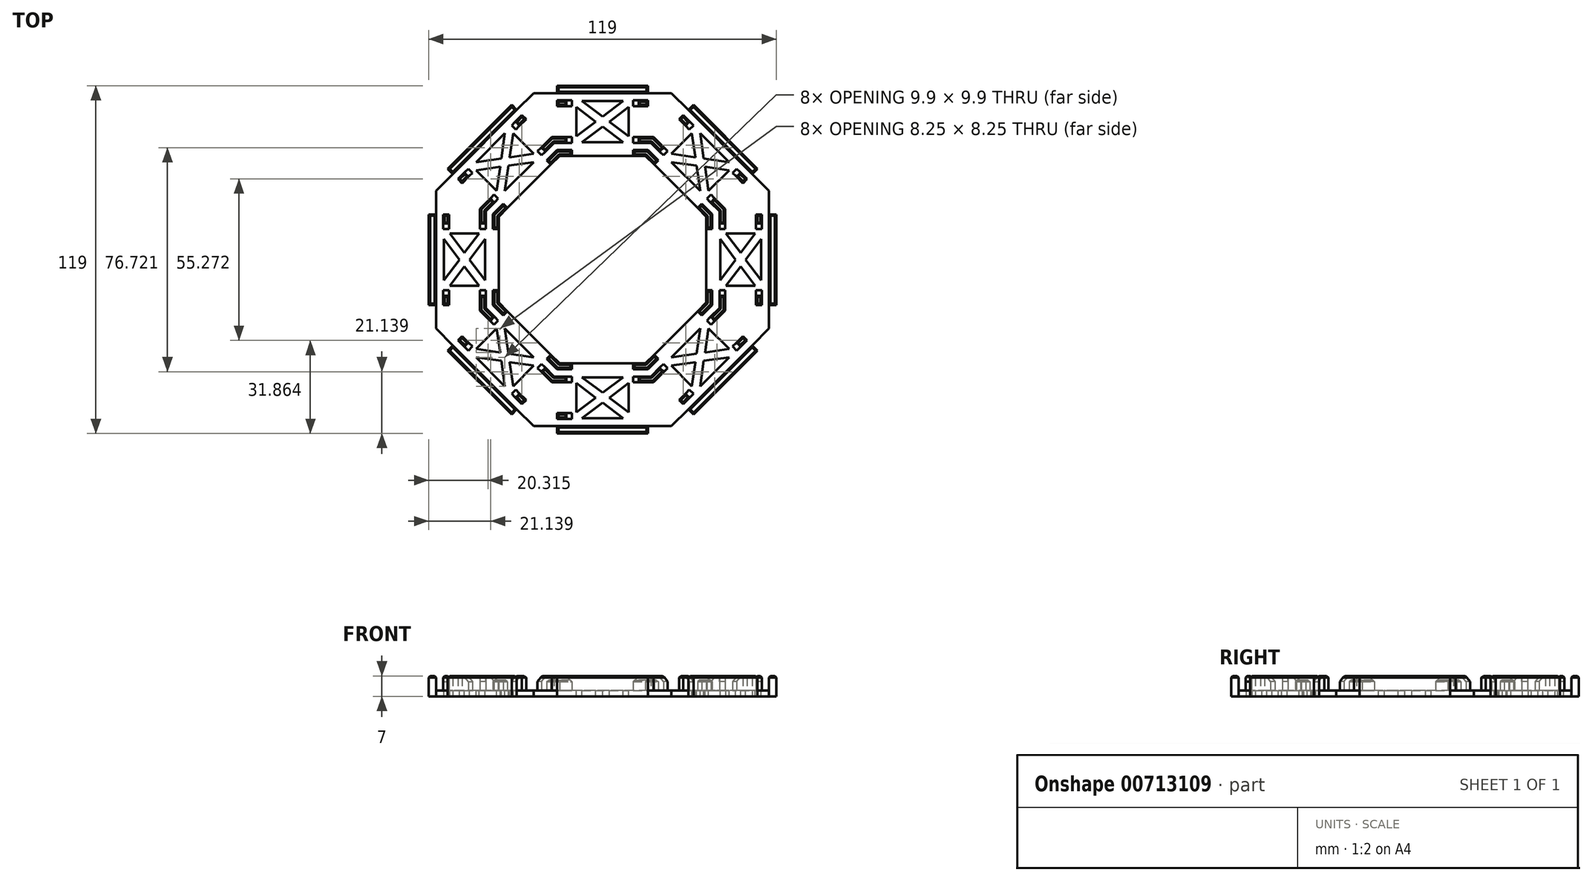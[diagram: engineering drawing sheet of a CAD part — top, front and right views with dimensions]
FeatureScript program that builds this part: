
annotation { "Feature Type Name" : "Feature", "Feature Type Description" : "" }
export const myFeature = defineFeature(function(context is Context, id is Id, definition is map)
    precondition{}
    {
        {
            var Q0;
            Q0=qCreatedBy(makeId("Top.planeOp"),FACE);
            var sketch = newSketch(context, id + "F0", { "sketchPlane" : qUnion([Q0])});
            skLineSegment(sketch, "E0.bottom", {"start": v(15.53, 37.5) * mm, "end": v(-15.53, 37.5) * mm});
            skLineSegment(sketch, "E0.top", {"start": v(15.53, -37.5) * mm, "end": v(-15.53, -37.5) * mm});
            skLineSegment(sketch, "E0.left", {"start": v(37.5, 15.53) * mm, "end": v(37.5, -15.53) * mm});
            skLineSegment(sketch, "E0.right", {"start": v(-37.5, 15.53) * mm, "end": v(-37.5, -15.53) * mm});
            skPoint(sketch, "E0.middle", {"position": v(0, 0) * mm});
            skLineSegment(sketch, "E1.bottom", {"start": v(37.5, 15.53) * mm, "end": v(15.53, 37.5) * mm});
            skLineSegment(sketch, "E1.top", {"start": v(-15.53, -37.5) * mm, "end": v(-37.5, -15.53) * mm});
            skLineSegment(sketch, "E1.left", {"start": v(37.5, -15.53) * mm, "end": v(15.53, -37.5) * mm});
            skLineSegment(sketch, "E1.right", {"start": v(-15.53, 37.5) * mm, "end": v(-37.5, 15.53) * mm});
            skPoint(sketch, "E2.orphan", {"position": v(-37.5, 37.5) * mm});
            skPoint(sketch, "E3.orphan", {"position": v(0, 53.03) * mm});
            skPoint(sketch, "E4.orphan", {"position": v(37.5, 37.5) * mm});
            skPoint(sketch, "E5.orphan", {"position": v(53.03, 0) * mm});
            skPoint(sketch, "E6.orphan", {"position": v(37.5, -37.5) * mm});
            skPoint(sketch, "E7.orphan", {"position": v(0, -53.03) * mm});
            skPoint(sketch, "E8.orphan", {"position": v(-37.5, -37.5) * mm});
            skPoint(sketch, "E9.orphan", {"position": v(-53.03, 0) * mm});
            skLineSegment(sketch, "E10.0", {"start": v(57, 23.61) * mm, "end": v(57, -23.61) * mm});
            skLineSegment(sketch, "E10.1", {"start": v(57, 23.61) * mm, "end": v(23.61, 57) * mm});
            skLineSegment(sketch, "E10.2", {"start": v(57, -23.61) * mm, "end": v(23.61, -57) * mm});
            skLineSegment(sketch, "E10.3", {"start": v(23.61, 57) * mm, "end": v(-23.61, 57) * mm});
            skLineSegment(sketch, "E10.4", {"start": v(23.61, -57) * mm, "end": v(-23.61, -57) * mm});
            skLineSegment(sketch, "E10.5", {"start": v(-23.61, -57) * mm, "end": v(-57, -23.61) * mm});
            skLineSegment(sketch, "E10.6", {"start": v(-57, 23.61) * mm, "end": v(-57, -23.61) * mm});
            skLineSegment(sketch, "E10.7", {"start": v(-23.61, 57) * mm, "end": v(-57, 23.61) * mm});
            skLineSegment(sketch, "E11.0", {"start": v(-16.57, 40) * mm, "end": v(-40, 16.57) * mm});
            skLineSegment(sketch, "E11.1", {"start": v(16.57, 40) * mm, "end": v(-16.57, 40) * mm});
            skLineSegment(sketch, "E11.2", {"start": v(-40, 16.57) * mm, "end": v(-40, -16.57) * mm});
            skLineSegment(sketch, "E11.3", {"start": v(40, 16.57) * mm, "end": v(16.57, 40) * mm});
            skLineSegment(sketch, "E11.4", {"start": v(-16.57, -40) * mm, "end": v(-40, -16.57) * mm});
            skLineSegment(sketch, "E11.5", {"start": v(16.57, -40) * mm, "end": v(-16.57, -40) * mm});
            skLineSegment(sketch, "E11.6", {"start": v(40, -16.57) * mm, "end": v(16.57, -40) * mm});
            skLineSegment(sketch, "E11.7", {"start": v(40, 16.57) * mm, "end": v(40, -16.57) * mm});
            skLineSegment(sketch, "E12.0", {"start": v(14.7, 35.5) * mm, "end": v(-14.7, 35.5) * mm});
            skLineSegment(sketch, "E12.1", {"start": v(35.5, 14.7) * mm, "end": v(14.7, 35.5) * mm});
            skLineSegment(sketch, "E12.2", {"start": v(-14.7, 35.5) * mm, "end": v(-35.5, 14.7) * mm});
            skLineSegment(sketch, "E12.3", {"start": v(35.5, 14.7) * mm, "end": v(35.5, -14.7) * mm});
            skLineSegment(sketch, "E12.4", {"start": v(-35.5, 14.7) * mm, "end": v(-35.5, -14.7) * mm});
            skLineSegment(sketch, "E12.5", {"start": v(-14.7, -35.5) * mm, "end": v(-35.5, -14.7) * mm});
            skLineSegment(sketch, "E12.6", {"start": v(14.7, -35.5) * mm, "end": v(-14.7, -35.5) * mm});
            skLineSegment(sketch, "E12.7", {"start": v(35.5, -14.7) * mm, "end": v(14.7, -35.5) * mm});
            skLineSegment(sketch, "E13.0", {"start": v(-17.4, 42) * mm, "end": v(-42, 17.4) * mm});
            skLineSegment(sketch, "E13.1", {"start": v(17.4, 42) * mm, "end": v(-17.4, 42) * mm});
            skLineSegment(sketch, "E13.2", {"start": v(-42, 17.4) * mm, "end": v(-42, -17.4) * mm});
            skLineSegment(sketch, "E13.3", {"start": v(42, 17.4) * mm, "end": v(17.4, 42) * mm});
            skLineSegment(sketch, "E13.4", {"start": v(-17.4, -42) * mm, "end": v(-42, -17.4) * mm});
            skLineSegment(sketch, "E13.5", {"start": v(17.4, -42) * mm, "end": v(-17.4, -42) * mm});
            skLineSegment(sketch, "E13.6", {"start": v(42, -17.4) * mm, "end": v(17.4, -42) * mm});
            skLineSegment(sketch, "E13.7", {"start": v(42, 17.4) * mm, "end": v(42, -17.4) * mm});
            skLineSegment(sketch, "E14.bottom", {"start": v(-10.5, -34.32) * mm, "end": v(10.5, -34.32) * mm});
            skLineSegment(sketch, "E14.top", {"start": v(-10.5, -45.68) * mm, "end": v(10.5, -45.68) * mm});
            skLineSegment(sketch, "E14.left", {"start": v(-10.5, -34.32) * mm, "end": v(-10.5, -45.68) * mm});
            skLineSegment(sketch, "E14.right", {"start": v(10.5, -34.32) * mm, "end": v(10.5, -45.68) * mm});
            skPoint(sketch, "E14.middle", {"position": v(0, -40) * mm});
            skLineSegment(sketch, "E15.1.0", {"start": v(16.85, -31.7) * mm, "end": v(31.7, -16.85) * mm});
            skLineSegment(sketch, "E15.1.1", {"start": v(16.85, -31.7) * mm, "end": v(24.87, -39.72) * mm});
            skLineSegment(sketch, "E15.1.2", {"start": v(24.87, -39.72) * mm, "end": v(39.72, -24.87) * mm});
            skLineSegment(sketch, "E15.1.3", {"start": v(31.7, -16.85) * mm, "end": v(39.72, -24.87) * mm});
            skLineSegment(sketch, "E15.2.0", {"start": v(34.32, -10.5) * mm, "end": v(34.32, 10.5) * mm});
            skLineSegment(sketch, "E15.2.1", {"start": v(34.32, -10.5) * mm, "end": v(45.68, -10.5) * mm});
            skLineSegment(sketch, "E15.2.2", {"start": v(45.68, -10.5) * mm, "end": v(45.68, 10.5) * mm});
            skLineSegment(sketch, "E15.2.3", {"start": v(34.32, 10.5) * mm, "end": v(45.68, 10.5) * mm});
            skLineSegment(sketch, "E16.1.3.0", {"start": v(31.7, 16.85) * mm, "end": v(16.85, 31.7) * mm});
            skLineSegment(sketch, "E16.3.3.0", {"start": v(31.7, 16.85) * mm, "end": v(39.72, 24.87) * mm});
            skLineSegment(sketch, "E16.6.3.0", {"start": v(39.72, 24.87) * mm, "end": v(24.87, 39.72) * mm});
            skLineSegment(sketch, "E16.9.3.0", {"start": v(16.85, 31.7) * mm, "end": v(24.87, 39.72) * mm});
            skLineSegment(sketch, "E16.1.4.0", {"start": v(10.5, 34.32) * mm, "end": v(-10.5, 34.32) * mm});
            skLineSegment(sketch, "E16.3.4.0", {"start": v(10.5, 34.32) * mm, "end": v(10.5, 45.68) * mm});
            skLineSegment(sketch, "E16.6.4.0", {"start": v(10.5, 45.68) * mm, "end": v(-10.5, 45.68) * mm});
            skLineSegment(sketch, "E16.9.4.0", {"start": v(-10.5, 34.32) * mm, "end": v(-10.5, 45.68) * mm});
            skLineSegment(sketch, "E16.1.5.0", {"start": v(-16.85, 31.7) * mm, "end": v(-31.7, 16.85) * mm});
            skLineSegment(sketch, "E16.3.5.0", {"start": v(-16.85, 31.7) * mm, "end": v(-24.87, 39.72) * mm});
            skLineSegment(sketch, "E16.6.5.0", {"start": v(-24.87, 39.72) * mm, "end": v(-39.72, 24.87) * mm});
            skLineSegment(sketch, "E16.9.5.0", {"start": v(-31.7, 16.85) * mm, "end": v(-39.72, 24.87) * mm});
            skLineSegment(sketch, "E16.1.6.0", {"start": v(-34.32, 10.5) * mm, "end": v(-34.32, -10.5) * mm});
            skLineSegment(sketch, "E16.3.6.0", {"start": v(-34.32, 10.5) * mm, "end": v(-45.68, 10.5) * mm});
            skLineSegment(sketch, "E16.6.6.0", {"start": v(-45.68, 10.5) * mm, "end": v(-45.68, -10.5) * mm});
            skLineSegment(sketch, "E16.9.6.0", {"start": v(-34.32, -10.5) * mm, "end": v(-45.68, -10.5) * mm});
            skLineSegment(sketch, "E16.1.7.0", {"start": v(-31.7, -16.85) * mm, "end": v(-16.85, -31.7) * mm});
            skLineSegment(sketch, "E16.3.7.0", {"start": v(-31.7, -16.85) * mm, "end": v(-39.72, -24.87) * mm});
            skLineSegment(sketch, "E16.6.7.0", {"start": v(-39.72, -24.87) * mm, "end": v(-24.87, -39.72) * mm});
            skLineSegment(sketch, "E16.9.7.0", {"start": v(-16.85, -31.7) * mm, "end": v(-24.87, -39.72) * mm});
            skSolve(sketch);
        }
        {
            var Q0;
            {var subQ0=sQuery(id+"F0.wireOp",EDGE,"E16.3.5.0");var subQ1=sQuery(id+"F0.wireOp",EDGE,"E11.0");var subQ2=makeQuery(id+"F0.imprint","INTERSECT",VERTEX,{"derivedFrom":[subQ1,subQ0]});Q0=makeQuery(id+"F0.imprint","IMPRINT",FACE,{"disambiguationData":[TD([[makeQuery(id+"F0.imprint","IMPRINT",EDGE,{"disambiguationData":[TD([[subQ2,-1.0]])],"derivedFrom":subQ1}),-1.0]])]});}
            var Q1;
            {var subQ0=sQuery(id+"F0.wireOp",EDGE,"E15.2.3");var subQ1=sQuery(id+"F0.wireOp",EDGE,"E0.left");var subQ2=makeQuery(id+"F0.imprint","INTERSECT",VERTEX,{"derivedFrom":[subQ1,subQ0]});Q1=makeQuery(id+"F0.imprint","IMPRINT",FACE,{"disambiguationData":[TD([[makeQuery(id+"F0.imprint","IMPRINT",EDGE,{"disambiguationData":[TD([[subQ2,-1.0]])],"derivedFrom":subQ1}),-1.0]])]});}
            var Q2;
            {var subQ5=sQuery(id+"F0.wireOp",EDGE,"E1.bottom");var subQ6=sQuery(id+"F0.wireOp",EDGE,"E0.left");var subQ7=makeQuery(id+"F0.imprint","INTERSECT",VERTEX,{"derivedFrom":[subQ6,subQ5]});Q2=makeQuery(id+"F0.imprint","IMPRINT",FACE,{"disambiguationData":[TD([[makeQuery(id+"F0.imprint","IMPRINT",EDGE,{"disambiguationData":[TD([[subQ7,-1.0]])],"derivedFrom":subQ6}),1.0]])]});}
            var Q3;
            {var subQ0=sQuery(id+"F0.wireOp",EDGE,"E16.3.3.0");var subQ1=sQuery(id+"F0.wireOp",EDGE,"E11.3");var subQ2=makeQuery(id+"F0.imprint","INTERSECT",VERTEX,{"derivedFrom":[subQ1,subQ0]});Q3=makeQuery(id+"F0.imprint","IMPRINT",FACE,{"disambiguationData":[TD([[makeQuery(id+"F0.imprint","IMPRINT",EDGE,{"disambiguationData":[TD([[subQ2,-1.0]])],"derivedFrom":subQ1}),-1.0]])]});}
            var Q4;
            {var subQ0=sQuery(id+"F0.wireOp",EDGE,"E16.3.3.0");var subQ1=sQuery(id+"F0.wireOp",EDGE,"E1.bottom");var subQ2=makeQuery(id+"F0.imprint","INTERSECT",VERTEX,{"derivedFrom":[subQ1,subQ0]});Q4=makeQuery(id+"F0.imprint","IMPRINT",FACE,{"disambiguationData":[TD([[makeQuery(id+"F0.imprint","IMPRINT",EDGE,{"disambiguationData":[TD([[subQ2,-1.0]])],"derivedFrom":subQ1}),1.0]])]});}
            var Q5;
            {var subQ0=sQuery(id+"F0.wireOp",EDGE,"E16.3.3.0");var subQ1=sQuery(id+"F0.wireOp",EDGE,"E1.bottom");var subQ2=makeQuery(id+"F0.imprint","INTERSECT",VERTEX,{"derivedFrom":[subQ1,subQ0]});Q5=makeQuery(id+"F0.imprint","IMPRINT",FACE,{"disambiguationData":[TD([[makeQuery(id+"F0.imprint","IMPRINT",EDGE,{"disambiguationData":[TD([[subQ2,-1.0]])],"derivedFrom":subQ1}),-1.0]])]});}
            var Q6;
            {var subQ5=sQuery(id+"F0.wireOp",EDGE,"E16.6.6.0");Q6=makeQuery(id+"F0.imprint","IMPRINT",FACE,{"disambiguationData":[TD([[makeQuery(id+"F0.imprint","IMPRINT",EDGE,{"derivedFrom":subQ5}),1.0]])]});}
            var Q7;
            {var subQ5=sQuery(id+"F0.wireOp",EDGE,"E0.right");var subQ7=sQuery(id+"F0.wireOp",EDGE,"E1.right");var subQ8=makeQuery(id+"F0.imprint","INTERSECT",VERTEX,{"derivedFrom":[subQ5,subQ7]});Q7=makeQuery(id+"F0.imprint","IMPRINT",FACE,{"disambiguationData":[TD([[makeQuery(id+"F0.imprint","IMPRINT",EDGE,{"disambiguationData":[TD([[subQ8,-1.0]])],"derivedFrom":subQ5}),1.0]])]});}
            var Q8;
            {var subQ0=sQuery(id+"F0.wireOp",EDGE,"E16.3.5.0");var subQ1=sQuery(id+"F0.wireOp",EDGE,"E1.right");var subQ2=makeQuery(id+"F0.imprint","INTERSECT",VERTEX,{"derivedFrom":[subQ1,subQ0]});Q8=makeQuery(id+"F0.imprint","IMPRINT",FACE,{"disambiguationData":[TD([[makeQuery(id+"F0.imprint","IMPRINT",EDGE,{"disambiguationData":[TD([[subQ2,-1.0]])],"derivedFrom":subQ1}),1.0]])]});}
            var Q9;
            {var subQ5=sQuery(id+"F0.wireOp",EDGE,"E15.2.2");Q9=makeQuery(id+"F0.imprint","IMPRINT",FACE,{"disambiguationData":[TD([[makeQuery(id+"F0.imprint","IMPRINT",EDGE,{"derivedFrom":subQ5}),1.0]])]});}
            var Q10;
            {var subQ0=sQuery(id+"F0.wireOp",EDGE,"E16.3.6.0");var subQ1=sQuery(id+"F0.wireOp",EDGE,"E11.2");var subQ2=makeQuery(id+"F0.imprint","INTERSECT",VERTEX,{"derivedFrom":[subQ1,subQ0]});Q10=makeQuery(id+"F0.imprint","IMPRINT",FACE,{"disambiguationData":[TD([[makeQuery(id+"F0.imprint","IMPRINT",EDGE,{"disambiguationData":[TD([[subQ2,-1.0]])],"derivedFrom":subQ1}),-1.0]])]});}
            var Q11;
            {var subQ7=sQuery(id+"F0.wireOp",EDGE,"E1.bottom");var subQ8=sQuery(id+"F0.wireOp",EDGE,"E0.bottom");var subQ9=makeQuery(id+"F0.imprint","INTERSECT",VERTEX,{"derivedFrom":[subQ8,subQ7]});Q11=makeQuery(id+"F0.imprint","IMPRINT",FACE,{"disambiguationData":[TD([[makeQuery(id+"F0.imprint","IMPRINT",EDGE,{"disambiguationData":[TD([[subQ9,-1.0]])],"derivedFrom":subQ8}),1.0]])]});}
            var Q12;
            {var subQ5=sQuery(id+"F0.wireOp",EDGE,"E16.6.4.0");Q12=makeQuery(id+"F0.imprint","IMPRINT",FACE,{"disambiguationData":[TD([[makeQuery(id+"F0.imprint","IMPRINT",EDGE,{"derivedFrom":subQ5}),1.0]])]});}
            var Q13;
            {var subQ0=sQuery(id+"F0.wireOp",EDGE,"E16.3.4.0");var subQ1=sQuery(id+"F0.wireOp",EDGE,"E11.1");var subQ2=makeQuery(id+"F0.imprint","INTERSECT",VERTEX,{"derivedFrom":[subQ1,subQ0]});Q13=makeQuery(id+"F0.imprint","IMPRINT",FACE,{"disambiguationData":[TD([[makeQuery(id+"F0.imprint","IMPRINT",EDGE,{"disambiguationData":[TD([[subQ2,-1.0]])],"derivedFrom":subQ1}),-1.0]])]});}
            var Q14;
            {var subQ5=sQuery(id+"F0.wireOp",EDGE,"E16.6.3.0");Q14=makeQuery(id+"F0.imprint","IMPRINT",FACE,{"disambiguationData":[TD([[makeQuery(id+"F0.imprint","IMPRINT",EDGE,{"derivedFrom":subQ5}),1.0]])]});}
            var Q15;
            {var subQ5=sQuery(id+"F0.wireOp",EDGE,"E1.right");var subQ6=sQuery(id+"F0.wireOp",EDGE,"E0.right");var subQ7=makeQuery(id+"F0.imprint","INTERSECT",VERTEX,{"derivedFrom":[subQ6,subQ5]});Q15=makeQuery(id+"F0.imprint","IMPRINT",FACE,{"disambiguationData":[TD([[makeQuery(id+"F0.imprint","IMPRINT",EDGE,{"disambiguationData":[TD([[subQ7,-1.0]])],"derivedFrom":subQ6}),-1.0]])]});}
            var Q16;
            {var subQ0=sQuery(id+"F0.wireOp",EDGE,"E16.3.4.0");var subQ1=sQuery(id+"F0.wireOp",EDGE,"E0.bottom");var subQ2=makeQuery(id+"F0.imprint","INTERSECT",VERTEX,{"derivedFrom":[subQ1,subQ0]});Q16=makeQuery(id+"F0.imprint","IMPRINT",FACE,{"disambiguationData":[TD([[makeQuery(id+"F0.imprint","IMPRINT",EDGE,{"disambiguationData":[TD([[subQ2,-1.0]])],"derivedFrom":subQ1}),1.0]])]});}
            var Q17;
            {var subQ0=sQuery(id+"F0.wireOp",EDGE,"E16.3.6.0");var subQ1=sQuery(id+"F0.wireOp",EDGE,"E0.right");var subQ2=makeQuery(id+"F0.imprint","INTERSECT",VERTEX,{"derivedFrom":[subQ1,subQ0]});Q17=makeQuery(id+"F0.imprint","IMPRINT",FACE,{"disambiguationData":[TD([[makeQuery(id+"F0.imprint","IMPRINT",EDGE,{"disambiguationData":[TD([[subQ2,-1.0]])],"derivedFrom":subQ1}),1.0]])]});}
            var Q18;
            {var subQ6=sQuery(id+"F0.wireOp",EDGE,"E11.0");var subQ9=sQuery(id+"F0.wireOp",EDGE,"E11.2");var subQ10=makeQuery(id+"F0.imprint","INTERSECT",VERTEX,{"derivedFrom":[subQ6,subQ9]});Q18=makeQuery(id+"F0.imprint","IMPRINT",FACE,{"disambiguationData":[TD([[makeQuery(id+"F0.imprint","IMPRINT",EDGE,{"disambiguationData":[TD([[subQ10,1.0]])],"derivedFrom":subQ6}),-1.0]])]});}
            var Q19;
            {var subQ0=sQuery(id+"F0.wireOp",EDGE,"E16.3.4.0");var subQ1=sQuery(id+"F0.wireOp",EDGE,"E0.bottom");var subQ2=makeQuery(id+"F0.imprint","INTERSECT",VERTEX,{"derivedFrom":[subQ1,subQ0]});Q19=makeQuery(id+"F0.imprint","IMPRINT",FACE,{"disambiguationData":[TD([[makeQuery(id+"F0.imprint","IMPRINT",EDGE,{"disambiguationData":[TD([[subQ2,-1.0]])],"derivedFrom":subQ1}),-1.0]])]});}
            var Q20;
            {var subQ0=sQuery(id+"F0.wireOp",EDGE,"E1.right");var subQ1=sQuery(id+"F0.wireOp",EDGE,"E0.bottom");var subQ2=makeQuery(id+"F0.imprint","INTERSECT",VERTEX,{"derivedFrom":[subQ1,subQ0]});Q20=makeQuery(id+"F0.imprint","IMPRINT",FACE,{"disambiguationData":[TD([[makeQuery(id+"F0.imprint","IMPRINT",EDGE,{"disambiguationData":[TD([[subQ2,1.0]])],"derivedFrom":subQ1}),-1.0]])]});}
            var Q21;
            {var subQ7=sQuery(id+"F0.wireOp",EDGE,"E11.3");var subQ8=sQuery(id+"F0.wireOp",EDGE,"E11.1");var subQ9=makeQuery(id+"F0.imprint","INTERSECT",VERTEX,{"derivedFrom":[subQ8,subQ7]});Q21=makeQuery(id+"F0.imprint","IMPRINT",FACE,{"disambiguationData":[TD([[makeQuery(id+"F0.imprint","IMPRINT",EDGE,{"disambiguationData":[TD([[subQ9,-1.0]])],"derivedFrom":subQ8}),-1.0]])]});}
            var Q22;
            {var subQ5=sQuery(id+"F0.wireOp",EDGE,"E11.1");var subQ9=sQuery(id+"F0.wireOp",EDGE,"E11.0");var subQ11=makeQuery(id+"F0.imprint","INTERSECT",VERTEX,{"derivedFrom":[subQ9,subQ5]});Q22=makeQuery(id+"F0.imprint","IMPRINT",FACE,{"disambiguationData":[TD([[makeQuery(id+"F0.imprint","IMPRINT",EDGE,{"disambiguationData":[TD([[subQ11,-1.0]])],"derivedFrom":subQ9}),-1.0]])]});}
            var Q23;
            {var subQ5=sQuery(id+"F0.wireOp",EDGE,"E1.bottom");var subQ6=sQuery(id+"F0.wireOp",EDGE,"E0.bottom");var subQ7=makeQuery(id+"F0.imprint","INTERSECT",VERTEX,{"derivedFrom":[subQ6,subQ5]});Q23=makeQuery(id+"F0.imprint","IMPRINT",FACE,{"disambiguationData":[TD([[makeQuery(id+"F0.imprint","IMPRINT",EDGE,{"disambiguationData":[TD([[subQ7,-1.0]])],"derivedFrom":subQ6}),-1.0]])]});}
            var Q24;
            {var subQ0=sQuery(id+"F0.wireOp",EDGE,"E16.3.5.0");var subQ1=sQuery(id+"F0.wireOp",EDGE,"E1.right");var subQ2=makeQuery(id+"F0.imprint","INTERSECT",VERTEX,{"derivedFrom":[subQ1,subQ0]});Q24=makeQuery(id+"F0.imprint","IMPRINT",FACE,{"disambiguationData":[TD([[makeQuery(id+"F0.imprint","IMPRINT",EDGE,{"disambiguationData":[TD([[subQ2,-1.0]])],"derivedFrom":subQ1}),-1.0]])]});}
            var Q25;
            {var subQ5=sQuery(id+"F0.wireOp",EDGE,"E11.3");var subQ7=sQuery(id+"F0.wireOp",EDGE,"E11.7");var subQ8=makeQuery(id+"F0.imprint","INTERSECT",VERTEX,{"derivedFrom":[subQ5,subQ7]});Q25=makeQuery(id+"F0.imprint","IMPRINT",FACE,{"disambiguationData":[TD([[makeQuery(id+"F0.imprint","IMPRINT",EDGE,{"disambiguationData":[TD([[subQ8,-1.0]])],"derivedFrom":subQ5}),-1.0]])]});}
            var Q26;
            {var subQ0=sQuery(id+"F0.wireOp",EDGE,"E15.2.3");var subQ1=sQuery(id+"F0.wireOp",EDGE,"E11.7");var subQ2=makeQuery(id+"F0.imprint","INTERSECT",VERTEX,{"derivedFrom":[subQ1,subQ0]});Q26=makeQuery(id+"F0.imprint","IMPRINT",FACE,{"disambiguationData":[TD([[makeQuery(id+"F0.imprint","IMPRINT",EDGE,{"disambiguationData":[TD([[subQ2,-1.0]])],"derivedFrom":subQ1}),1.0]])]});}
            var Q27;
            {var subQ5=sQuery(id+"F0.wireOp",EDGE,"E16.6.5.0");Q27=makeQuery(id+"F0.imprint","IMPRINT",FACE,{"disambiguationData":[TD([[makeQuery(id+"F0.imprint","IMPRINT",EDGE,{"derivedFrom":subQ5}),1.0]])]});}
            var Q28;
            Q28=makeQuery(id+"F0.imprint","IMPRINT",FACE,{"disambiguationData":[TD([[makeQuery(id+"F0.imprint","IMPRINT",EDGE,{"derivedFrom":sQuery(id+"F0.wireOp",EDGE,"E10.0")}),-1.0]])]});
            var Q29;
            {var subQ0=sQuery(id+"F0.wireOp",EDGE,"E15.2.3");var subQ1=sQuery(id+"F0.wireOp",EDGE,"E0.left");var subQ2=makeQuery(id+"F0.imprint","INTERSECT",VERTEX,{"derivedFrom":[subQ1,subQ0]});Q29=makeQuery(id+"F0.imprint","IMPRINT",FACE,{"disambiguationData":[TD([[makeQuery(id+"F0.imprint","IMPRINT",EDGE,{"disambiguationData":[TD([[subQ2,-1.0]])],"derivedFrom":subQ1}),1.0]])]});}
            var Q30;
            {var subQ6=sQuery(id+"F0.wireOp",EDGE,"E1.bottom");var subQ9=sQuery(id+"F0.wireOp",EDGE,"E0.left");var subQ11=makeQuery(id+"F0.imprint","INTERSECT",VERTEX,{"derivedFrom":[subQ9,subQ6]});Q30=makeQuery(id+"F0.imprint","IMPRINT",FACE,{"disambiguationData":[TD([[makeQuery(id+"F0.imprint","IMPRINT",EDGE,{"disambiguationData":[TD([[subQ11,-1.0]])],"derivedFrom":subQ9}),-1.0]])]});}
            var Q31;
            {var subQ0=sQuery(id+"F0.wireOp",EDGE,"E16.3.6.0");var subQ1=sQuery(id+"F0.wireOp",EDGE,"E0.right");var subQ2=makeQuery(id+"F0.imprint","INTERSECT",VERTEX,{"derivedFrom":[subQ1,subQ0]});Q31=makeQuery(id+"F0.imprint","IMPRINT",FACE,{"disambiguationData":[TD([[makeQuery(id+"F0.imprint","IMPRINT",EDGE,{"disambiguationData":[TD([[subQ2,-1.0]])],"derivedFrom":subQ1}),-1.0]])]});}
            var Q32;
            {var subQ5=sQuery(id+"F0.wireOp",EDGE,"E1.right");var subQ6=sQuery(id+"F0.wireOp",EDGE,"E0.bottom");var subQ7=makeQuery(id+"F0.imprint","INTERSECT",VERTEX,{"derivedFrom":[subQ6,subQ5]});Q32=makeQuery(id+"F0.imprint","IMPRINT",FACE,{"disambiguationData":[TD([[makeQuery(id+"F0.imprint","IMPRINT",EDGE,{"disambiguationData":[TD([[subQ7,1.0]])],"derivedFrom":subQ6}),1.0]])]});}
            var Q33;
            {var subQ5=sQuery(id+"F0.wireOp",EDGE,"E14.top");Q33=makeQuery(id+"F0.imprint","IMPRINT",FACE,{"disambiguationData":[TD([[makeQuery(id+"F0.imprint","IMPRINT",EDGE,{"derivedFrom":subQ5}),1.0]])]});}
            var Q34;
            {var subQ0=sQuery(id+"F0.wireOp",EDGE,"E14.right");var subQ1=sQuery(id+"F0.wireOp",EDGE,"E0.top");var subQ2=makeQuery(id+"F0.imprint","INTERSECT",VERTEX,{"derivedFrom":[subQ1,subQ0]});Q34=makeQuery(id+"F0.imprint","IMPRINT",FACE,{"disambiguationData":[TD([[makeQuery(id+"F0.imprint","IMPRINT",EDGE,{"disambiguationData":[TD([[subQ2,-1.0]])],"derivedFrom":subQ1}),1.0]])]});}
            var Q35;
            {var subQ0=sQuery(id+"F0.wireOp",EDGE,"E16.9.7.0");var subQ1=sQuery(id+"F0.wireOp",EDGE,"E1.top");var subQ2=makeQuery(id+"F0.imprint","INTERSECT",VERTEX,{"derivedFrom":[subQ1,subQ0]});Q35=makeQuery(id+"F0.imprint","IMPRINT",FACE,{"disambiguationData":[TD([[makeQuery(id+"F0.imprint","IMPRINT",EDGE,{"disambiguationData":[TD([[subQ2,-1.0]])],"derivedFrom":subQ1}),1.0]])]});}
            var Q36;
            {var subQ0=sQuery(id+"F0.wireOp",EDGE,"E16.9.7.0");var subQ1=sQuery(id+"F0.wireOp",EDGE,"E11.4");var subQ2=makeQuery(id+"F0.imprint","INTERSECT",VERTEX,{"derivedFrom":[subQ1,subQ0]});Q36=makeQuery(id+"F0.imprint","IMPRINT",FACE,{"disambiguationData":[TD([[makeQuery(id+"F0.imprint","IMPRINT",EDGE,{"disambiguationData":[TD([[subQ2,-1.0]])],"derivedFrom":subQ1}),1.0]])]});}
            var Q37;
            {var subQ6=sQuery(id+"F0.wireOp",EDGE,"E0.top");var subQ9=sQuery(id+"F0.wireOp",EDGE,"E1.left");var subQ11=makeQuery(id+"F0.imprint","INTERSECT",VERTEX,{"derivedFrom":[subQ6,subQ9]});Q37=makeQuery(id+"F0.imprint","IMPRINT",FACE,{"disambiguationData":[TD([[makeQuery(id+"F0.imprint","IMPRINT",EDGE,{"disambiguationData":[TD([[subQ11,-1.0]])],"derivedFrom":subQ6}),-1.0]])]});}
            var Q38;
            {var subQ7=sQuery(id+"F0.wireOp",EDGE,"E1.top");var subQ8=sQuery(id+"F0.wireOp",EDGE,"E0.right");var subQ9=makeQuery(id+"F0.imprint","INTERSECT",VERTEX,{"derivedFrom":[subQ8,subQ7]});Q38=makeQuery(id+"F0.imprint","IMPRINT",FACE,{"disambiguationData":[TD([[makeQuery(id+"F0.imprint","IMPRINT",EDGE,{"disambiguationData":[TD([[subQ9,1.0]])],"derivedFrom":subQ8}),1.0]])]});}
            var Q39;
            {var subQ7=sQuery(id+"F0.wireOp",EDGE,"E11.4");var subQ8=sQuery(id+"F0.wireOp",EDGE,"E11.2");var subQ9=makeQuery(id+"F0.imprint","INTERSECT",VERTEX,{"derivedFrom":[subQ8,subQ7]});Q39=makeQuery(id+"F0.imprint","IMPRINT",FACE,{"disambiguationData":[TD([[makeQuery(id+"F0.imprint","IMPRINT",EDGE,{"disambiguationData":[TD([[subQ9,1.0]])],"derivedFrom":subQ8}),-1.0]])]});}
            var Q40;
            {var subQ7=sQuery(id+"F0.wireOp",EDGE,"E11.6");var subQ8=sQuery(id+"F0.wireOp",EDGE,"E11.5");var subQ9=makeQuery(id+"F0.imprint","INTERSECT",VERTEX,{"derivedFrom":[subQ8,subQ7]});Q40=makeQuery(id+"F0.imprint","IMPRINT",FACE,{"disambiguationData":[TD([[makeQuery(id+"F0.imprint","IMPRINT",EDGE,{"disambiguationData":[TD([[subQ9,-1.0]])],"derivedFrom":subQ8}),1.0]])]});}
            var Q41;
            {var subQ5=sQuery(id+"F0.wireOp",EDGE,"E16.6.7.0");Q41=makeQuery(id+"F0.imprint","IMPRINT",FACE,{"disambiguationData":[TD([[makeQuery(id+"F0.imprint","IMPRINT",EDGE,{"derivedFrom":subQ5}),1.0]])]});}
            var Q42;
            {var subQ0=sQuery(id+"F0.wireOp",EDGE,"E14.right");var subQ1=sQuery(id+"F0.wireOp",EDGE,"E0.top");var subQ2=makeQuery(id+"F0.imprint","INTERSECT",VERTEX,{"derivedFrom":[subQ1,subQ0]});Q42=makeQuery(id+"F0.imprint","IMPRINT",FACE,{"disambiguationData":[TD([[makeQuery(id+"F0.imprint","IMPRINT",EDGE,{"disambiguationData":[TD([[subQ2,-1.0]])],"derivedFrom":subQ1}),-1.0]])]});}
            var Q43;
            {var subQ0=sQuery(id+"F0.wireOp",EDGE,"E16.9.7.0");var subQ1=sQuery(id+"F0.wireOp",EDGE,"E1.top");var subQ2=makeQuery(id+"F0.imprint","INTERSECT",VERTEX,{"derivedFrom":[subQ1,subQ0]});Q43=makeQuery(id+"F0.imprint","IMPRINT",FACE,{"disambiguationData":[TD([[makeQuery(id+"F0.imprint","IMPRINT",EDGE,{"disambiguationData":[TD([[subQ2,-1.0]])],"derivedFrom":subQ1}),-1.0]])]});}
            var Q44;
            {var subQ7=sQuery(id+"F0.wireOp",EDGE,"E1.left");var subQ8=sQuery(id+"F0.wireOp",EDGE,"E0.left");var subQ9=makeQuery(id+"F0.imprint","INTERSECT",VERTEX,{"derivedFrom":[subQ8,subQ7]});Q44=makeQuery(id+"F0.imprint","IMPRINT",FACE,{"disambiguationData":[TD([[makeQuery(id+"F0.imprint","IMPRINT",EDGE,{"disambiguationData":[TD([[subQ9,1.0]])],"derivedFrom":subQ8}),-1.0]])]});}
            var Q45;
            {var subQ7=sQuery(id+"F0.wireOp",EDGE,"E1.top");var subQ8=sQuery(id+"F0.wireOp",EDGE,"E0.top");var subQ9=makeQuery(id+"F0.imprint","INTERSECT",VERTEX,{"derivedFrom":[subQ8,subQ7]});Q45=makeQuery(id+"F0.imprint","IMPRINT",FACE,{"disambiguationData":[TD([[makeQuery(id+"F0.imprint","IMPRINT",EDGE,{"disambiguationData":[TD([[subQ9,1.0]])],"derivedFrom":subQ8}),-1.0]])]});}
            var Q46;
            {var subQ0=sQuery(id+"F0.wireOp",EDGE,"E15.1.3");var subQ1=sQuery(id+"F0.wireOp",EDGE,"E1.left");var subQ2=makeQuery(id+"F0.imprint","INTERSECT",VERTEX,{"derivedFrom":[subQ1,subQ0]});Q46=makeQuery(id+"F0.imprint","IMPRINT",FACE,{"disambiguationData":[TD([[makeQuery(id+"F0.imprint","IMPRINT",EDGE,{"disambiguationData":[TD([[subQ2,-1.0]])],"derivedFrom":subQ1}),1.0]])]});}
            var Q47;
            {var subQ7=sQuery(id+"F0.wireOp",EDGE,"E1.left");var subQ8=sQuery(id+"F0.wireOp",EDGE,"E0.top");var subQ9=makeQuery(id+"F0.imprint","INTERSECT",VERTEX,{"derivedFrom":[subQ8,subQ7]});Q47=makeQuery(id+"F0.imprint","IMPRINT",FACE,{"disambiguationData":[TD([[makeQuery(id+"F0.imprint","IMPRINT",EDGE,{"disambiguationData":[TD([[subQ9,-1.0]])],"derivedFrom":subQ8}),1.0]])]});}
            var Q48;
            {var subQ5=sQuery(id+"F0.wireOp",EDGE,"E1.top");var subQ6=sQuery(id+"F0.wireOp",EDGE,"E0.right");var subQ7=makeQuery(id+"F0.imprint","INTERSECT",VERTEX,{"derivedFrom":[subQ6,subQ5]});Q48=makeQuery(id+"F0.imprint","IMPRINT",FACE,{"disambiguationData":[TD([[makeQuery(id+"F0.imprint","IMPRINT",EDGE,{"disambiguationData":[TD([[subQ7,1.0]])],"derivedFrom":subQ6}),-1.0]])]});}
            var Q49;
            {var subQ5=sQuery(id+"F0.wireOp",EDGE,"E15.1.2");Q49=makeQuery(id+"F0.imprint","IMPRINT",FACE,{"disambiguationData":[TD([[makeQuery(id+"F0.imprint","IMPRINT",EDGE,{"derivedFrom":subQ5}),1.0]])]});}
            var Q50;
            {var subQ7=sQuery(id+"F0.wireOp",EDGE,"E1.left");var subQ8=sQuery(id+"F0.wireOp",EDGE,"E0.left");var subQ9=makeQuery(id+"F0.imprint","INTERSECT",VERTEX,{"derivedFrom":[subQ8,subQ7]});Q50=makeQuery(id+"F0.imprint","IMPRINT",FACE,{"disambiguationData":[TD([[makeQuery(id+"F0.imprint","IMPRINT",EDGE,{"disambiguationData":[TD([[subQ9,1.0]])],"derivedFrom":subQ8}),1.0]])]});}
            var Q51;
            {var subQ7=sQuery(id+"F0.wireOp",EDGE,"E11.7");var subQ8=sQuery(id+"F0.wireOp",EDGE,"E11.6");var subQ9=makeQuery(id+"F0.imprint","INTERSECT",VERTEX,{"derivedFrom":[subQ8,subQ7]});Q51=makeQuery(id+"F0.imprint","IMPRINT",FACE,{"disambiguationData":[TD([[makeQuery(id+"F0.imprint","IMPRINT",EDGE,{"disambiguationData":[TD([[subQ9,-1.0]])],"derivedFrom":subQ8}),1.0]])]});}
            var Q52;
            {var subQ0=sQuery(id+"F0.wireOp",EDGE,"E15.1.3");var subQ1=sQuery(id+"F0.wireOp",EDGE,"E1.left");var subQ2=makeQuery(id+"F0.imprint","INTERSECT",VERTEX,{"derivedFrom":[subQ1,subQ0]});Q52=makeQuery(id+"F0.imprint","IMPRINT",FACE,{"disambiguationData":[TD([[makeQuery(id+"F0.imprint","IMPRINT",EDGE,{"disambiguationData":[TD([[subQ2,-1.0]])],"derivedFrom":subQ1}),-1.0]])]});}
            var Q53;
            {var subQ0=sQuery(id+"F0.wireOp",EDGE,"E15.1.3");var subQ1=sQuery(id+"F0.wireOp",EDGE,"E11.6");var subQ2=makeQuery(id+"F0.imprint","INTERSECT",VERTEX,{"derivedFrom":[subQ1,subQ0]});Q53=makeQuery(id+"F0.imprint","IMPRINT",FACE,{"disambiguationData":[TD([[makeQuery(id+"F0.imprint","IMPRINT",EDGE,{"disambiguationData":[TD([[subQ2,-1.0]])],"derivedFrom":subQ1}),1.0]])]});}
            var Q54;
            {var subQ7=sQuery(id+"F0.wireOp",EDGE,"E11.5");var subQ8=sQuery(id+"F0.wireOp",EDGE,"E11.4");var subQ9=makeQuery(id+"F0.imprint","INTERSECT",VERTEX,{"derivedFrom":[subQ8,subQ7]});Q54=makeQuery(id+"F0.imprint","IMPRINT",FACE,{"disambiguationData":[TD([[makeQuery(id+"F0.imprint","IMPRINT",EDGE,{"disambiguationData":[TD([[subQ9,-1.0]])],"derivedFrom":subQ8}),1.0]])]});}
            var Q55;
            {var subQ5=sQuery(id+"F0.wireOp",EDGE,"E1.top");var subQ6=sQuery(id+"F0.wireOp",EDGE,"E0.top");var subQ7=makeQuery(id+"F0.imprint","INTERSECT",VERTEX,{"derivedFrom":[subQ6,subQ5]});Q55=makeQuery(id+"F0.imprint","IMPRINT",FACE,{"disambiguationData":[TD([[makeQuery(id+"F0.imprint","IMPRINT",EDGE,{"disambiguationData":[TD([[subQ7,1.0]])],"derivedFrom":subQ6}),1.0]])]});}
            var Q56;
            {var subQ0=sQuery(id+"F0.wireOp",EDGE,"E14.right");var subQ1=sQuery(id+"F0.wireOp",EDGE,"E11.5");var subQ2=makeQuery(id+"F0.imprint","INTERSECT",VERTEX,{"derivedFrom":[subQ1,subQ0]});Q56=makeQuery(id+"F0.imprint","IMPRINT",FACE,{"disambiguationData":[TD([[makeQuery(id+"F0.imprint","IMPRINT",EDGE,{"disambiguationData":[TD([[subQ2,-1.0]])],"derivedFrom":subQ1}),1.0]])]});}
            extrude(context, id + "F1", {"entities" : qUnion([Q0, Q1, Q2, Q3, Q4, Q5, Q6, Q7, Q8, Q9, Q10, Q11, Q12, Q13, Q14, Q15, Q16, Q17, Q18, Q19, Q20, Q21, Q22, Q23, Q24, Q25, Q26, Q27, Q28, Q29, Q30, Q31, Q32, Q33, Q34, Q35, Q36, Q37, Q38, Q39, Q40, Q41, Q42, Q43, Q44, Q45, Q46, Q47, Q48, Q49, Q50, Q51, Q52, Q53, Q54, Q55, Q56]), "depth" : 2 * mm, "offsetDistance" : 25 * mm});
        }
        {
            var Q0;
            {var subQ7=sQuery(id+"F0.wireOp",EDGE,"E1.left");var subQ8=sQuery(id+"F0.wireOp",EDGE,"E0.left");var subQ9=makeQuery(id+"F0.imprint","INTERSECT",VERTEX,{"derivedFrom":[subQ8,subQ7]});Q0=makeQuery(id+"F0.imprint","IMPRINT",FACE,{"disambiguationData":[TD([[makeQuery(id+"F0.imprint","IMPRINT",EDGE,{"disambiguationData":[TD([[subQ9,1.0]])],"derivedFrom":subQ8}),-1.0]])]});}
            var Q1;
            {var subQ6=sQuery(id+"F0.wireOp",EDGE,"E0.top");var subQ9=sQuery(id+"F0.wireOp",EDGE,"E1.left");var subQ11=makeQuery(id+"F0.imprint","INTERSECT",VERTEX,{"derivedFrom":[subQ6,subQ9]});Q1=makeQuery(id+"F0.imprint","IMPRINT",FACE,{"disambiguationData":[TD([[makeQuery(id+"F0.imprint","IMPRINT",EDGE,{"disambiguationData":[TD([[subQ11,-1.0]])],"derivedFrom":subQ6}),-1.0]])]});}
            var Q2;
            {var subQ7=sQuery(id+"F0.wireOp",EDGE,"E1.top");var subQ8=sQuery(id+"F0.wireOp",EDGE,"E0.top");var subQ9=makeQuery(id+"F0.imprint","INTERSECT",VERTEX,{"derivedFrom":[subQ8,subQ7]});Q2=makeQuery(id+"F0.imprint","IMPRINT",FACE,{"disambiguationData":[TD([[makeQuery(id+"F0.imprint","IMPRINT",EDGE,{"disambiguationData":[TD([[subQ9,1.0]])],"derivedFrom":subQ8}),-1.0]])]});}
            var Q3;
            {var subQ7=sQuery(id+"F0.wireOp",EDGE,"E1.top");var subQ8=sQuery(id+"F0.wireOp",EDGE,"E0.right");var subQ9=makeQuery(id+"F0.imprint","INTERSECT",VERTEX,{"derivedFrom":[subQ8,subQ7]});Q3=makeQuery(id+"F0.imprint","IMPRINT",FACE,{"disambiguationData":[TD([[makeQuery(id+"F0.imprint","IMPRINT",EDGE,{"disambiguationData":[TD([[subQ9,1.0]])],"derivedFrom":subQ8}),1.0]])]});}
            var Q4;
            {var subQ5=sQuery(id+"F0.wireOp",EDGE,"E0.right");var subQ7=sQuery(id+"F0.wireOp",EDGE,"E1.right");var subQ8=makeQuery(id+"F0.imprint","INTERSECT",VERTEX,{"derivedFrom":[subQ5,subQ7]});Q4=makeQuery(id+"F0.imprint","IMPRINT",FACE,{"disambiguationData":[TD([[makeQuery(id+"F0.imprint","IMPRINT",EDGE,{"disambiguationData":[TD([[subQ8,-1.0]])],"derivedFrom":subQ5}),1.0]])]});}
            var Q5;
            {var subQ5=sQuery(id+"F0.wireOp",EDGE,"E1.right");var subQ6=sQuery(id+"F0.wireOp",EDGE,"E0.bottom");var subQ7=makeQuery(id+"F0.imprint","INTERSECT",VERTEX,{"derivedFrom":[subQ6,subQ5]});Q5=makeQuery(id+"F0.imprint","IMPRINT",FACE,{"disambiguationData":[TD([[makeQuery(id+"F0.imprint","IMPRINT",EDGE,{"disambiguationData":[TD([[subQ7,1.0]])],"derivedFrom":subQ6}),1.0]])]});}
            var Q6;
            {var subQ7=sQuery(id+"F0.wireOp",EDGE,"E1.bottom");var subQ8=sQuery(id+"F0.wireOp",EDGE,"E0.bottom");var subQ9=makeQuery(id+"F0.imprint","INTERSECT",VERTEX,{"derivedFrom":[subQ8,subQ7]});Q6=makeQuery(id+"F0.imprint","IMPRINT",FACE,{"disambiguationData":[TD([[makeQuery(id+"F0.imprint","IMPRINT",EDGE,{"disambiguationData":[TD([[subQ9,-1.0]])],"derivedFrom":subQ8}),1.0]])]});}
            var Q7;
            {var subQ6=sQuery(id+"F0.wireOp",EDGE,"E1.bottom");var subQ9=sQuery(id+"F0.wireOp",EDGE,"E0.left");var subQ11=makeQuery(id+"F0.imprint","INTERSECT",VERTEX,{"derivedFrom":[subQ9,subQ6]});Q7=makeQuery(id+"F0.imprint","IMPRINT",FACE,{"disambiguationData":[TD([[makeQuery(id+"F0.imprint","IMPRINT",EDGE,{"disambiguationData":[TD([[subQ11,-1.0]])],"derivedFrom":subQ9}),-1.0]])]});}
            extrude(context, id + "F2", {"entities" : qUnion([Q0, Q1, Q2, Q3, Q4, Q5, Q6, Q7]), "operationType" : NewBodyOperationType.ADD, "depth" : 5.5 * mm, "offsetDistance" : 25 * mm});
        }
        {
            var Q0;
            {var subQ7=sQuery(id+"F0.wireOp",EDGE,"E11.5");var subQ8=sQuery(id+"F0.wireOp",EDGE,"E11.4");var subQ9=makeQuery(id+"F0.imprint","INTERSECT",VERTEX,{"derivedFrom":[subQ8,subQ7]});Q0=makeQuery(id+"F0.imprint","IMPRINT",FACE,{"disambiguationData":[TD([[makeQuery(id+"F0.imprint","IMPRINT",EDGE,{"disambiguationData":[TD([[subQ9,-1.0]])],"derivedFrom":subQ8}),1.0]])]});}
            var Q1;
            {var subQ7=sQuery(id+"F0.wireOp",EDGE,"E11.6");var subQ8=sQuery(id+"F0.wireOp",EDGE,"E11.5");var subQ9=makeQuery(id+"F0.imprint","INTERSECT",VERTEX,{"derivedFrom":[subQ8,subQ7]});Q1=makeQuery(id+"F0.imprint","IMPRINT",FACE,{"disambiguationData":[TD([[makeQuery(id+"F0.imprint","IMPRINT",EDGE,{"disambiguationData":[TD([[subQ9,-1.0]])],"derivedFrom":subQ8}),1.0]])]});}
            var Q2;
            {var subQ7=sQuery(id+"F0.wireOp",EDGE,"E11.7");var subQ8=sQuery(id+"F0.wireOp",EDGE,"E11.6");var subQ9=makeQuery(id+"F0.imprint","INTERSECT",VERTEX,{"derivedFrom":[subQ8,subQ7]});Q2=makeQuery(id+"F0.imprint","IMPRINT",FACE,{"disambiguationData":[TD([[makeQuery(id+"F0.imprint","IMPRINT",EDGE,{"disambiguationData":[TD([[subQ9,-1.0]])],"derivedFrom":subQ8}),1.0]])]});}
            var Q3;
            {var subQ5=sQuery(id+"F0.wireOp",EDGE,"E11.3");var subQ7=sQuery(id+"F0.wireOp",EDGE,"E11.7");var subQ8=makeQuery(id+"F0.imprint","INTERSECT",VERTEX,{"derivedFrom":[subQ5,subQ7]});Q3=makeQuery(id+"F0.imprint","IMPRINT",FACE,{"disambiguationData":[TD([[makeQuery(id+"F0.imprint","IMPRINT",EDGE,{"disambiguationData":[TD([[subQ8,-1.0]])],"derivedFrom":subQ5}),-1.0]])]});}
            var Q4;
            {var subQ7=sQuery(id+"F0.wireOp",EDGE,"E11.3");var subQ8=sQuery(id+"F0.wireOp",EDGE,"E11.1");var subQ9=makeQuery(id+"F0.imprint","INTERSECT",VERTEX,{"derivedFrom":[subQ8,subQ7]});Q4=makeQuery(id+"F0.imprint","IMPRINT",FACE,{"disambiguationData":[TD([[makeQuery(id+"F0.imprint","IMPRINT",EDGE,{"disambiguationData":[TD([[subQ9,-1.0]])],"derivedFrom":subQ8}),-1.0]])]});}
            var Q5;
            {var subQ5=sQuery(id+"F0.wireOp",EDGE,"E11.1");var subQ9=sQuery(id+"F0.wireOp",EDGE,"E11.0");var subQ11=makeQuery(id+"F0.imprint","INTERSECT",VERTEX,{"derivedFrom":[subQ9,subQ5]});Q5=makeQuery(id+"F0.imprint","IMPRINT",FACE,{"disambiguationData":[TD([[makeQuery(id+"F0.imprint","IMPRINT",EDGE,{"disambiguationData":[TD([[subQ11,-1.0]])],"derivedFrom":subQ9}),-1.0]])]});}
            var Q6;
            {var subQ6=sQuery(id+"F0.wireOp",EDGE,"E11.0");var subQ9=sQuery(id+"F0.wireOp",EDGE,"E11.2");var subQ10=makeQuery(id+"F0.imprint","INTERSECT",VERTEX,{"derivedFrom":[subQ6,subQ9]});Q6=makeQuery(id+"F0.imprint","IMPRINT",FACE,{"disambiguationData":[TD([[makeQuery(id+"F0.imprint","IMPRINT",EDGE,{"disambiguationData":[TD([[subQ10,1.0]])],"derivedFrom":subQ6}),-1.0]])]});}
            var Q7;
            {var subQ7=sQuery(id+"F0.wireOp",EDGE,"E11.4");var subQ8=sQuery(id+"F0.wireOp",EDGE,"E11.2");var subQ9=makeQuery(id+"F0.imprint","INTERSECT",VERTEX,{"derivedFrom":[subQ8,subQ7]});Q7=makeQuery(id+"F0.imprint","IMPRINT",FACE,{"disambiguationData":[TD([[makeQuery(id+"F0.imprint","IMPRINT",EDGE,{"disambiguationData":[TD([[subQ9,1.0]])],"derivedFrom":subQ8}),-1.0]])]});}
            extrude(context, id + "F3", {"entities" : qUnion([Q0, Q1, Q2, Q3, Q4, Q5, Q6, Q7]), "operationType" : NewBodyOperationType.ADD, "depth" : 7 * mm, "offsetDistance" : 25 * mm});
        }
        {
            var Q0;
            Q0=makeQuery(id+"F1.opExtrude","CAP_FACE",FACE,{"disambiguationData":[OSD([sQuery(id+"F0.wireOp",EDGE,"E10.0"),sQuery(id+"F0.wireOp",EDGE,"E10.1"),sQuery(id+"F0.wireOp",EDGE,"E10.2"),sQuery(id+"F0.wireOp",EDGE,"E10.3"),sQuery(id+"F0.wireOp",EDGE,"E10.4"),sQuery(id+"F0.wireOp",EDGE,"E10.5"),sQuery(id+"F0.wireOp",EDGE,"E10.6"),sQuery(id+"F0.wireOp",EDGE,"E10.7"),sQuery(id+"F0.wireOp",EDGE,"E12.0"),sQuery(id+"F0.wireOp",EDGE,"E12.1"),sQuery(id+"F0.wireOp",EDGE,"E12.2"),sQuery(id+"F0.wireOp",EDGE,"E12.3"),sQuery(id+"F0.wireOp",EDGE,"E12.4"),sQuery(id+"F0.wireOp",EDGE,"E12.5"),sQuery(id+"F0.wireOp",EDGE,"E12.6"),sQuery(id+"F0.wireOp",EDGE,"E12.7")])],"isStart":false});
            var sketch = newSketch(context, id + "F4", { "sketchPlane" : qUnion([Q0])});
            skLineSegment(sketch, "E17.bottom", {"start": v(-10.5, -54.5) * mm, "end": v(10.5, -54.5) * mm});
            skLineSegment(sketch, "E17.top", {"start": v(-10.5, -59.5) * mm, "end": v(10.5, -59.5) * mm});
            skLineSegment(sketch, "E17.left", {"start": v(-10.5, -54.5) * mm, "end": v(-10.5, -59.5) * mm});
            skLineSegment(sketch, "E17.right", {"start": v(10.5, -54.5) * mm, "end": v(10.5, -59.5) * mm});
            skPoint(sketch, "E17.middle", {"position": v(0, -57) * mm});
            skLineSegment(sketch, "E18.bottom", {"start": v(10.5, -59.5) * mm, "end": v(15.5, -59.5) * mm});
            skLineSegment(sketch, "E18.top", {"start": v(10.5, -54.5) * mm, "end": v(15.5, -54.5) * mm});
            skLineSegment(sketch, "E18.left", {"start": v(10.5, -59.5) * mm, "end": v(10.5, -54.5) * mm});
            skLineSegment(sketch, "E18.right", {"start": v(15.5, -59.5) * mm, "end": v(15.5, -54.5) * mm});
            skLineSegment(sketch, "E19.bottom", {"start": v(-10.5, -59.5) * mm, "end": v(-15.5, -59.5) * mm});
            skLineSegment(sketch, "E19.top", {"start": v(-10.5, -54.5) * mm, "end": v(-15.5, -54.5) * mm});
            skLineSegment(sketch, "E19.left", {"start": v(-10.5, -59.5) * mm, "end": v(-10.5, -54.5) * mm});
            skLineSegment(sketch, "E19.right", {"start": v(-15.5, -59.5) * mm, "end": v(-15.5, -54.5) * mm});
            skLineSegment(sketch, "E20.bottom", {"start": v(15.5, -54.5) * mm, "end": v(10.5, -54.5) * mm});
            skLineSegment(sketch, "E20.top", {"start": v(15.5, -52.5) * mm, "end": v(10.5, -52.5) * mm});
            skLineSegment(sketch, "E20.left", {"start": v(15.5, -54.5) * mm, "end": v(15.5, -52.5) * mm});
            skLineSegment(sketch, "E20.right", {"start": v(10.5, -54.5) * mm, "end": v(10.5, -52.5) * mm});
            skPoint(sketch, "E21.oppositeSnap0", {"position": v(13, -52.5) * mm});
            skLineSegment(sketch, "E21.top", {"start": v(-10.5, -52.5) * mm, "end": v(-15.5, -52.5) * mm});
            skLineSegment(sketch, "E21.left", {"start": v(-10.5, -54.5) * mm, "end": v(-10.5, -52.5) * mm});
            skLineSegment(sketch, "E21.right", {"start": v(-15.5, -54.5) * mm, "end": v(-15.5, -52.5) * mm});
            skLineSegment(sketch, "E22.1.0", {"start": v(49.5, -27.58) * mm, "end": v(48.08, -26.16) * mm});
            skLineSegment(sketch, "E22.1.1", {"start": v(49.5, -27.58) * mm, "end": v(45.96, -31.11) * mm});
            skLineSegment(sketch, "E22.1.2", {"start": v(29.7, -44.55) * mm, "end": v(26.16, -48.08) * mm});
            skLineSegment(sketch, "E22.1.3", {"start": v(48.08, -26.16) * mm, "end": v(44.55, -29.7) * mm});
            skLineSegment(sketch, "E22.1.4", {"start": v(49.5, -34.65) * mm, "end": v(45.96, -31.11) * mm});
            skLineSegment(sketch, "E22.1.5", {"start": v(31.11, -45.96) * mm, "end": v(45.96, -31.11) * mm});
            skPoint(sketch, "E22.1.6", {"position": v(46.32, -27.93) * mm});
            skLineSegment(sketch, "E22.1.7", {"start": v(49.5, -34.65) * mm, "end": v(53.03, -31.11) * mm});
            skLineSegment(sketch, "E22.1.8", {"start": v(34.65, -49.5) * mm, "end": v(31.11, -53.03) * mm});
            skLineSegment(sketch, "E22.1.9", {"start": v(34.65, -49.5) * mm, "end": v(49.5, -34.65) * mm});
            skLineSegment(sketch, "E22.1.10", {"start": v(31.11, -45.96) * mm, "end": v(27.58, -49.5) * mm});
            skLineSegment(sketch, "E22.1.11", {"start": v(53.03, -31.11) * mm, "end": v(49.5, -27.58) * mm});
            skLineSegment(sketch, "E22.1.12", {"start": v(34.65, -49.5) * mm, "end": v(31.11, -45.96) * mm});
            skLineSegment(sketch, "E22.1.13", {"start": v(45.96, -31.11) * mm, "end": v(44.55, -29.7) * mm});
            skLineSegment(sketch, "E22.1.14", {"start": v(31.11, -53.03) * mm, "end": v(27.58, -49.5) * mm});
            skLineSegment(sketch, "E22.1.15", {"start": v(31.11, -45.96) * mm, "end": v(29.7, -44.55) * mm});
            skLineSegment(sketch, "E22.1.16", {"start": v(27.58, -49.5) * mm, "end": v(26.16, -48.08) * mm});
            skPoint(sketch, "E22.1.17", {"position": v(40.3, -40.3) * mm});
            skLineSegment(sketch, "E22.1.18", {"start": v(31.11, -45.96) * mm, "end": v(34.65, -49.5) * mm});
            skLineSegment(sketch, "E22.1.19", {"start": v(45.96, -31.11) * mm, "end": v(49.5, -27.58) * mm});
            skLineSegment(sketch, "E22.1.20", {"start": v(31.11, -45.96) * mm, "end": v(27.58, -49.5) * mm});
            skLineSegment(sketch, "E22.1.21", {"start": v(45.96, -31.11) * mm, "end": v(49.5, -34.65) * mm});
            skLineSegment(sketch, "E22.2.0", {"start": v(54.5, 15.5) * mm, "end": v(52.5, 15.5) * mm});
            skLineSegment(sketch, "E22.2.1", {"start": v(54.5, 15.5) * mm, "end": v(54.5, 10.5) * mm});
            skLineSegment(sketch, "E22.2.2", {"start": v(52.5, -10.5) * mm, "end": v(52.5, -15.5) * mm});
            skLineSegment(sketch, "E22.2.3", {"start": v(52.5, 15.5) * mm, "end": v(52.5, 10.5) * mm});
            skLineSegment(sketch, "E22.2.4", {"start": v(59.5, 10.5) * mm, "end": v(54.5, 10.5) * mm});
            skLineSegment(sketch, "E22.2.5", {"start": v(54.5, -10.5) * mm, "end": v(54.5, 10.5) * mm});
            skPoint(sketch, "E22.2.6", {"position": v(52.5, 13) * mm});
            skLineSegment(sketch, "E22.2.7", {"start": v(59.5, 10.5) * mm, "end": v(59.5, 15.5) * mm});
            skLineSegment(sketch, "E22.2.8", {"start": v(59.5, -10.5) * mm, "end": v(59.5, -15.5) * mm});
            skLineSegment(sketch, "E22.2.9", {"start": v(59.5, -10.5) * mm, "end": v(59.5, 10.5) * mm});
            skLineSegment(sketch, "E22.2.10", {"start": v(54.5, -10.5) * mm, "end": v(54.5, -15.5) * mm});
            skLineSegment(sketch, "E22.2.11", {"start": v(59.5, 15.5) * mm, "end": v(54.5, 15.5) * mm});
            skLineSegment(sketch, "E22.2.12", {"start": v(59.5, -10.5) * mm, "end": v(54.5, -10.5) * mm});
            skLineSegment(sketch, "E22.2.13", {"start": v(54.5, 10.5) * mm, "end": v(52.5, 10.5) * mm});
            skLineSegment(sketch, "E22.2.14", {"start": v(59.5, -15.5) * mm, "end": v(54.5, -15.5) * mm});
            skLineSegment(sketch, "E22.2.15", {"start": v(54.5, -10.5) * mm, "end": v(52.5, -10.5) * mm});
            skLineSegment(sketch, "E22.2.16", {"start": v(54.5, -15.5) * mm, "end": v(52.5, -15.5) * mm});
            skPoint(sketch, "E22.2.17", {"position": v(57, 0) * mm});
            skLineSegment(sketch, "E22.2.18", {"start": v(54.5, -10.5) * mm, "end": v(59.5, -10.5) * mm});
            skLineSegment(sketch, "E22.2.19", {"start": v(54.5, 10.5) * mm, "end": v(54.5, 15.5) * mm});
            skLineSegment(sketch, "E22.2.20", {"start": v(54.5, -10.5) * mm, "end": v(54.5, -15.5) * mm});
            skLineSegment(sketch, "E22.2.21", {"start": v(54.5, 10.5) * mm, "end": v(59.5, 10.5) * mm});
            skPoint(sketch, "E22.center", {"position": v(0, 0) * mm});
            skLineSegment(sketch, "E23.3.3.0", {"start": v(27.58, 49.5) * mm, "end": v(31.11, 45.96) * mm});
            skLineSegment(sketch, "E23.6.3.0", {"start": v(44.55, 29.7) * mm, "end": v(48.08, 26.16) * mm});
            skLineSegment(sketch, "E23.9.3.0", {"start": v(26.16, 48.08) * mm, "end": v(29.7, 44.55) * mm});
            skLineSegment(sketch, "E23.12.3.0", {"start": v(34.65, 49.5) * mm, "end": v(31.11, 45.96) * mm});
            skLineSegment(sketch, "E23.15.3.0", {"start": v(45.96, 31.11) * mm, "end": v(31.11, 45.96) * mm});
            skPoint(sketch, "E23.18.3.0", {"position": v(27.93, 46.32) * mm});
            skLineSegment(sketch, "E23.19.3.0", {"start": v(34.65, 49.5) * mm, "end": v(31.11, 53.03) * mm});
            skLineSegment(sketch, "E23.22.3.0", {"start": v(49.5, 34.65) * mm, "end": v(53.03, 31.11) * mm});
            skLineSegment(sketch, "E23.24.3.0", {"start": v(27.58, 49.5) * mm, "end": v(26.16, 48.08) * mm});
            skLineSegment(sketch, "E23.25.3.0", {"start": v(49.5, 34.65) * mm, "end": v(34.65, 49.5) * mm});
            skLineSegment(sketch, "E23.28.3.0", {"start": v(45.96, 31.11) * mm, "end": v(49.5, 27.58) * mm});
            skLineSegment(sketch, "E23.31.3.0", {"start": v(31.11, 53.03) * mm, "end": v(27.58, 49.5) * mm});
            skLineSegment(sketch, "E23.34.3.0", {"start": v(49.5, 34.65) * mm, "end": v(45.96, 31.11) * mm});
            skLineSegment(sketch, "E23.37.3.0", {"start": v(31.11, 45.96) * mm, "end": v(29.7, 44.55) * mm});
            skLineSegment(sketch, "E23.40.3.0", {"start": v(53.03, 31.11) * mm, "end": v(49.5, 27.58) * mm});
            skLineSegment(sketch, "E23.43.3.0", {"start": v(45.96, 31.11) * mm, "end": v(44.55, 29.7) * mm});
            skLineSegment(sketch, "E23.46.3.0", {"start": v(49.5, 27.58) * mm, "end": v(48.08, 26.16) * mm});
            skPoint(sketch, "E23.49.3.0", {"position": v(40.3, 40.3) * mm});
            skLineSegment(sketch, "E23.50.3.0", {"start": v(45.96, 31.11) * mm, "end": v(49.5, 34.65) * mm});
            skLineSegment(sketch, "E23.53.3.0", {"start": v(31.11, 45.96) * mm, "end": v(27.58, 49.5) * mm});
            skLineSegment(sketch, "E23.56.3.0", {"start": v(45.96, 31.11) * mm, "end": v(49.5, 27.58) * mm});
            skLineSegment(sketch, "E23.59.3.0", {"start": v(31.11, 45.96) * mm, "end": v(34.65, 49.5) * mm});
            skLineSegment(sketch, "E23.3.4.0", {"start": v(-15.5, 54.5) * mm, "end": v(-10.5, 54.5) * mm});
            skLineSegment(sketch, "E23.6.4.0", {"start": v(10.5, 52.5) * mm, "end": v(15.5, 52.5) * mm});
            skLineSegment(sketch, "E23.9.4.0", {"start": v(-15.5, 52.5) * mm, "end": v(-10.5, 52.5) * mm});
            skLineSegment(sketch, "E23.12.4.0", {"start": v(-10.5, 59.5) * mm, "end": v(-10.5, 54.5) * mm});
            skLineSegment(sketch, "E23.15.4.0", {"start": v(10.5, 54.5) * mm, "end": v(-10.5, 54.5) * mm});
            skPoint(sketch, "E23.18.4.0", {"position": v(-13, 52.5) * mm});
            skLineSegment(sketch, "E23.19.4.0", {"start": v(-10.5, 59.5) * mm, "end": v(-15.5, 59.5) * mm});
            skLineSegment(sketch, "E23.22.4.0", {"start": v(10.5, 59.5) * mm, "end": v(15.5, 59.5) * mm});
            skLineSegment(sketch, "E23.24.4.0", {"start": v(-15.5, 54.5) * mm, "end": v(-15.5, 52.5) * mm});
            skLineSegment(sketch, "E23.25.4.0", {"start": v(10.5, 59.5) * mm, "end": v(-10.5, 59.5) * mm});
            skLineSegment(sketch, "E23.28.4.0", {"start": v(10.5, 54.5) * mm, "end": v(15.5, 54.5) * mm});
            skLineSegment(sketch, "E23.31.4.0", {"start": v(-15.5, 59.5) * mm, "end": v(-15.5, 54.5) * mm});
            skLineSegment(sketch, "E23.34.4.0", {"start": v(10.5, 59.5) * mm, "end": v(10.5, 54.5) * mm});
            skLineSegment(sketch, "E23.37.4.0", {"start": v(-10.5, 54.5) * mm, "end": v(-10.5, 52.5) * mm});
            skLineSegment(sketch, "E23.40.4.0", {"start": v(15.5, 59.5) * mm, "end": v(15.5, 54.5) * mm});
            skLineSegment(sketch, "E23.43.4.0", {"start": v(10.5, 54.5) * mm, "end": v(10.5, 52.5) * mm});
            skLineSegment(sketch, "E23.46.4.0", {"start": v(15.5, 54.5) * mm, "end": v(15.5, 52.5) * mm});
            skPoint(sketch, "E23.49.4.0", {"position": v(0, 57) * mm});
            skLineSegment(sketch, "E23.50.4.0", {"start": v(10.5, 54.5) * mm, "end": v(10.5, 59.5) * mm});
            skLineSegment(sketch, "E23.53.4.0", {"start": v(-10.5, 54.5) * mm, "end": v(-15.5, 54.5) * mm});
            skLineSegment(sketch, "E23.56.4.0", {"start": v(10.5, 54.5) * mm, "end": v(15.5, 54.5) * mm});
            skLineSegment(sketch, "E23.59.4.0", {"start": v(-10.5, 54.5) * mm, "end": v(-10.5, 59.5) * mm});
            skLineSegment(sketch, "E23.3.5.0", {"start": v(-49.5, 27.58) * mm, "end": v(-45.96, 31.11) * mm});
            skLineSegment(sketch, "E23.6.5.0", {"start": v(-29.7, 44.55) * mm, "end": v(-26.16, 48.08) * mm});
            skLineSegment(sketch, "E23.9.5.0", {"start": v(-48.08, 26.16) * mm, "end": v(-44.55, 29.7) * mm});
            skLineSegment(sketch, "E23.12.5.0", {"start": v(-49.5, 34.65) * mm, "end": v(-45.96, 31.11) * mm});
            skLineSegment(sketch, "E23.15.5.0", {"start": v(-31.11, 45.96) * mm, "end": v(-45.96, 31.11) * mm});
            skPoint(sketch, "E23.18.5.0", {"position": v(-46.32, 27.93) * mm});
            skLineSegment(sketch, "E23.19.5.0", {"start": v(-49.5, 34.65) * mm, "end": v(-53.03, 31.11) * mm});
            skLineSegment(sketch, "E23.22.5.0", {"start": v(-34.65, 49.5) * mm, "end": v(-31.11, 53.03) * mm});
            skLineSegment(sketch, "E23.24.5.0", {"start": v(-49.5, 27.58) * mm, "end": v(-48.08, 26.16) * mm});
            skLineSegment(sketch, "E23.25.5.0", {"start": v(-34.65, 49.5) * mm, "end": v(-49.5, 34.65) * mm});
            skLineSegment(sketch, "E23.28.5.0", {"start": v(-31.11, 45.96) * mm, "end": v(-27.58, 49.5) * mm});
            skLineSegment(sketch, "E23.31.5.0", {"start": v(-53.03, 31.11) * mm, "end": v(-49.5, 27.58) * mm});
            skLineSegment(sketch, "E23.34.5.0", {"start": v(-34.65, 49.5) * mm, "end": v(-31.11, 45.96) * mm});
            skLineSegment(sketch, "E23.37.5.0", {"start": v(-45.96, 31.11) * mm, "end": v(-44.55, 29.7) * mm});
            skLineSegment(sketch, "E23.40.5.0", {"start": v(-31.11, 53.03) * mm, "end": v(-27.58, 49.5) * mm});
            skLineSegment(sketch, "E23.43.5.0", {"start": v(-31.11, 45.96) * mm, "end": v(-29.7, 44.55) * mm});
            skLineSegment(sketch, "E23.46.5.0", {"start": v(-27.58, 49.5) * mm, "end": v(-26.16, 48.08) * mm});
            skPoint(sketch, "E23.49.5.0", {"position": v(-40.3, 40.3) * mm});
            skLineSegment(sketch, "E23.50.5.0", {"start": v(-31.11, 45.96) * mm, "end": v(-34.65, 49.5) * mm});
            skLineSegment(sketch, "E23.53.5.0", {"start": v(-45.96, 31.11) * mm, "end": v(-49.5, 27.58) * mm});
            skLineSegment(sketch, "E23.56.5.0", {"start": v(-31.11, 45.96) * mm, "end": v(-27.58, 49.5) * mm});
            skLineSegment(sketch, "E23.59.5.0", {"start": v(-45.96, 31.11) * mm, "end": v(-49.5, 34.65) * mm});
            skLineSegment(sketch, "E23.3.6.0", {"start": v(-54.5, -15.5) * mm, "end": v(-54.5, -10.5) * mm});
            skLineSegment(sketch, "E23.6.6.0", {"start": v(-52.5, 10.5) * mm, "end": v(-52.5, 15.5) * mm});
            skLineSegment(sketch, "E23.9.6.0", {"start": v(-52.5, -15.5) * mm, "end": v(-52.5, -10.5) * mm});
            skLineSegment(sketch, "E23.12.6.0", {"start": v(-59.5, -10.5) * mm, "end": v(-54.5, -10.5) * mm});
            skLineSegment(sketch, "E23.15.6.0", {"start": v(-54.5, 10.5) * mm, "end": v(-54.5, -10.5) * mm});
            skPoint(sketch, "E23.18.6.0", {"position": v(-52.5, -13) * mm});
            skLineSegment(sketch, "E23.19.6.0", {"start": v(-59.5, -10.5) * mm, "end": v(-59.5, -15.5) * mm});
            skLineSegment(sketch, "E23.22.6.0", {"start": v(-59.5, 10.5) * mm, "end": v(-59.5, 15.5) * mm});
            skLineSegment(sketch, "E23.24.6.0", {"start": v(-54.5, -15.5) * mm, "end": v(-52.5, -15.5) * mm});
            skLineSegment(sketch, "E23.25.6.0", {"start": v(-59.5, 10.5) * mm, "end": v(-59.5, -10.5) * mm});
            skLineSegment(sketch, "E23.28.6.0", {"start": v(-54.5, 10.5) * mm, "end": v(-54.5, 15.5) * mm});
            skLineSegment(sketch, "E23.31.6.0", {"start": v(-59.5, -15.5) * mm, "end": v(-54.5, -15.5) * mm});
            skLineSegment(sketch, "E23.34.6.0", {"start": v(-59.5, 10.5) * mm, "end": v(-54.5, 10.5) * mm});
            skLineSegment(sketch, "E23.37.6.0", {"start": v(-54.5, -10.5) * mm, "end": v(-52.5, -10.5) * mm});
            skLineSegment(sketch, "E23.40.6.0", {"start": v(-59.5, 15.5) * mm, "end": v(-54.5, 15.5) * mm});
            skLineSegment(sketch, "E23.43.6.0", {"start": v(-54.5, 10.5) * mm, "end": v(-52.5, 10.5) * mm});
            skLineSegment(sketch, "E23.46.6.0", {"start": v(-54.5, 15.5) * mm, "end": v(-52.5, 15.5) * mm});
            skPoint(sketch, "E23.49.6.0", {"position": v(-57, 0) * mm});
            skLineSegment(sketch, "E23.50.6.0", {"start": v(-54.5, 10.5) * mm, "end": v(-59.5, 10.5) * mm});
            skLineSegment(sketch, "E23.53.6.0", {"start": v(-54.5, -10.5) * mm, "end": v(-54.5, -15.5) * mm});
            skLineSegment(sketch, "E23.56.6.0", {"start": v(-54.5, 10.5) * mm, "end": v(-54.5, 15.5) * mm});
            skLineSegment(sketch, "E23.59.6.0", {"start": v(-54.5, -10.5) * mm, "end": v(-59.5, -10.5) * mm});
            skLineSegment(sketch, "E23.3.7.0", {"start": v(-27.58, -49.5) * mm, "end": v(-31.11, -45.96) * mm});
            skLineSegment(sketch, "E23.6.7.0", {"start": v(-44.55, -29.7) * mm, "end": v(-48.08, -26.16) * mm});
            skLineSegment(sketch, "E23.9.7.0", {"start": v(-26.16, -48.08) * mm, "end": v(-29.7, -44.55) * mm});
            skLineSegment(sketch, "E23.12.7.0", {"start": v(-34.65, -49.5) * mm, "end": v(-31.11, -45.96) * mm});
            skLineSegment(sketch, "E23.15.7.0", {"start": v(-45.96, -31.11) * mm, "end": v(-31.11, -45.96) * mm});
            skPoint(sketch, "E23.18.7.0", {"position": v(-27.93, -46.32) * mm});
            skLineSegment(sketch, "E23.19.7.0", {"start": v(-34.65, -49.5) * mm, "end": v(-31.11, -53.03) * mm});
            skLineSegment(sketch, "E23.22.7.0", {"start": v(-49.5, -34.65) * mm, "end": v(-53.03, -31.11) * mm});
            skLineSegment(sketch, "E23.24.7.0", {"start": v(-27.58, -49.5) * mm, "end": v(-26.16, -48.08) * mm});
            skLineSegment(sketch, "E23.25.7.0", {"start": v(-49.5, -34.65) * mm, "end": v(-34.65, -49.5) * mm});
            skLineSegment(sketch, "E23.28.7.0", {"start": v(-45.96, -31.11) * mm, "end": v(-49.5, -27.58) * mm});
            skLineSegment(sketch, "E23.31.7.0", {"start": v(-31.11, -53.03) * mm, "end": v(-27.58, -49.5) * mm});
            skLineSegment(sketch, "E23.34.7.0", {"start": v(-49.5, -34.65) * mm, "end": v(-45.96, -31.11) * mm});
            skLineSegment(sketch, "E23.37.7.0", {"start": v(-31.11, -45.96) * mm, "end": v(-29.7, -44.55) * mm});
            skLineSegment(sketch, "E23.40.7.0", {"start": v(-53.03, -31.11) * mm, "end": v(-49.5, -27.58) * mm});
            skLineSegment(sketch, "E23.43.7.0", {"start": v(-45.96, -31.11) * mm, "end": v(-44.55, -29.7) * mm});
            skLineSegment(sketch, "E23.46.7.0", {"start": v(-49.5, -27.58) * mm, "end": v(-48.08, -26.16) * mm});
            skPoint(sketch, "E23.49.7.0", {"position": v(-40.3, -40.3) * mm});
            skLineSegment(sketch, "E23.50.7.0", {"start": v(-45.96, -31.11) * mm, "end": v(-49.5, -34.65) * mm});
            skLineSegment(sketch, "E23.53.7.0", {"start": v(-31.11, -45.96) * mm, "end": v(-27.58, -49.5) * mm});
            skLineSegment(sketch, "E23.56.7.0", {"start": v(-45.96, -31.11) * mm, "end": v(-49.5, -27.58) * mm});
            skLineSegment(sketch, "E23.59.7.0", {"start": v(-31.11, -45.96) * mm, "end": v(-34.65, -49.5) * mm});
            skLineSegment(sketch, "E24.bottom", {"start": v(-9, -54.25) * mm, "end": v(9, -54.25) * mm});
            skLineSegment(sketch, "E24.top", {"start": v(-9, -40.25) * mm, "end": v(9, -40.25) * mm});
            skLineSegment(sketch, "E24.left", {"start": v(-9, -54.25) * mm, "end": v(-9, -40.25) * mm});
            skLineSegment(sketch, "E24.right", {"start": v(9, -54.25) * mm, "end": v(9, -40.25) * mm});
            skPoint(sketch, "E24.middle", {"position": v(0, -47.25) * mm});
            skLineSegment(sketch, "E25.bottom", {"start": v(9, -54.25) * mm, "end": v(7, -54.25) * mm});
            skLineSegment(sketch, "E25.top", {"start": v(9, -52.25) * mm, "end": v(7, -52.25) * mm});
            skLineSegment(sketch, "E25.left", {"start": v(9, -54.25) * mm, "end": v(9, -52.25) * mm});
            skLineSegment(sketch, "E25.right", {"start": v(7, -54.25) * mm, "end": v(7, -52.25) * mm});
            skLineSegment(sketch, "E26.bottom", {"start": v(9, -40.25) * mm, "end": v(7, -40.25) * mm});
            skLineSegment(sketch, "E26.top", {"start": v(9, -42.25) * mm, "end": v(7, -42.25) * mm});
            skLineSegment(sketch, "E26.left", {"start": v(9, -40.25) * mm, "end": v(9, -42.25) * mm});
            skLineSegment(sketch, "E26.right", {"start": v(7, -40.25) * mm, "end": v(7, -42.25) * mm});
            skLineSegment(sketch, "E27.bottom", {"start": v(-9, -40.25) * mm, "end": v(-7, -40.25) * mm});
            skLineSegment(sketch, "E27.top", {"start": v(-9, -42.25) * mm, "end": v(-7, -42.25) * mm});
            skLineSegment(sketch, "E27.left", {"start": v(-9, -40.25) * mm, "end": v(-9, -42.25) * mm});
            skLineSegment(sketch, "E27.right", {"start": v(-7, -40.25) * mm, "end": v(-7, -42.25) * mm});
            skLineSegment(sketch, "E28.bottom", {"start": v(-9, -54.25) * mm, "end": v(-7, -54.25) * mm});
            skLineSegment(sketch, "E28.top", {"start": v(-9, -52.25) * mm, "end": v(-7, -52.25) * mm});
            skLineSegment(sketch, "E28.left", {"start": v(-9, -54.25) * mm, "end": v(-9, -52.25) * mm});
            skLineSegment(sketch, "E28.right", {"start": v(-7, -54.25) * mm, "end": v(-7, -52.25) * mm});
            skLineSegment(sketch, "E29", {"start": v(7, -40.25) * mm, "end": v(-9, -52.25) * mm});
            skLineSegment(sketch, "E30", {"start": v(-7, -54.25) * mm, "end": v(9, -42.25) * mm});
            skLineSegment(sketch, "E31", {"start": v(9, -52.25) * mm, "end": v(-7, -40.25) * mm});
            skLineSegment(sketch, "E32", {"start": v(7, -54.25) * mm, "end": v(-9, -42.25) * mm});
            skLineSegment(sketch, "E33", {"start": v(0, -57) * mm, "end": v(0, -47.25) * mm});
            skLineSegment(sketch, "E34.1.0", {"start": v(44.72, -32) * mm, "end": v(43.31, -33.41) * mm});
            skLineSegment(sketch, "E34.1.1", {"start": v(44.72, -32) * mm, "end": v(34.83, -22.1) * mm});
            skLineSegment(sketch, "E34.1.2", {"start": v(33.41, -43.31) * mm, "end": v(32, -41.9) * mm});
            skLineSegment(sketch, "E34.1.3", {"start": v(33.41, -23.51) * mm, "end": v(30.58, -43.31) * mm});
            skPoint(sketch, "E34.1.4", {"position": v(33.41, -33.41) * mm});
            skLineSegment(sketch, "E34.1.5", {"start": v(33.41, -43.31) * mm, "end": v(36.24, -23.51) * mm});
            skLineSegment(sketch, "E34.1.6", {"start": v(43.31, -30.58) * mm, "end": v(41.9, -32) * mm});
            skLineSegment(sketch, "E34.1.7", {"start": v(43.31, -30.58) * mm, "end": v(23.51, -33.41) * mm});
            skLineSegment(sketch, "E34.1.8", {"start": v(44.72, -32) * mm, "end": v(43.31, -30.58) * mm});
            skLineSegment(sketch, "E34.1.9", {"start": v(43.31, -33.41) * mm, "end": v(41.9, -32) * mm});
            skLineSegment(sketch, "E34.1.10", {"start": v(43.31, -33.41) * mm, "end": v(23.51, -36.24) * mm});
            skLineSegment(sketch, "E34.1.11", {"start": v(36.24, -23.51) * mm, "end": v(34.83, -24.93) * mm});
            skLineSegment(sketch, "E34.1.12", {"start": v(23.51, -36.24) * mm, "end": v(24.93, -34.83) * mm});
            skLineSegment(sketch, "E34.1.13", {"start": v(32, -44.72) * mm, "end": v(44.72, -32) * mm});
            skLineSegment(sketch, "E34.1.14", {"start": v(34.83, -22.1) * mm, "end": v(36.24, -23.51) * mm});
            skLineSegment(sketch, "E34.1.15", {"start": v(23.51, -33.41) * mm, "end": v(24.93, -34.83) * mm});
            skLineSegment(sketch, "E34.1.16", {"start": v(32, -44.72) * mm, "end": v(22.1, -34.83) * mm});
            skLineSegment(sketch, "E34.1.17", {"start": v(34.83, -22.1) * mm, "end": v(33.41, -23.51) * mm});
            skLineSegment(sketch, "E34.1.18", {"start": v(33.41, -23.51) * mm, "end": v(34.83, -24.93) * mm});
            skLineSegment(sketch, "E34.1.19", {"start": v(30.58, -43.31) * mm, "end": v(32, -41.9) * mm});
            skLineSegment(sketch, "E34.1.20", {"start": v(22.1, -34.83) * mm, "end": v(34.83, -22.1) * mm});
            skLineSegment(sketch, "E34.1.21", {"start": v(22.1, -34.83) * mm, "end": v(23.51, -33.41) * mm});
            skLineSegment(sketch, "E34.1.22", {"start": v(32, -44.72) * mm, "end": v(30.58, -43.31) * mm});
            skLineSegment(sketch, "E34.1.23", {"start": v(22.1, -34.83) * mm, "end": v(23.51, -36.24) * mm});
            skLineSegment(sketch, "E34.1.24", {"start": v(32, -44.72) * mm, "end": v(33.41, -43.31) * mm});
            skLineSegment(sketch, "E34.2.0", {"start": v(54.25, 9) * mm, "end": v(54.25, 7) * mm});
            skLineSegment(sketch, "E34.2.1", {"start": v(54.25, 9) * mm, "end": v(40.25, 9) * mm});
            skLineSegment(sketch, "E34.2.2", {"start": v(54.25, -7) * mm, "end": v(52.25, -7) * mm});
            skLineSegment(sketch, "E34.2.3", {"start": v(40.25, 7) * mm, "end": v(52.25, -9) * mm});
            skPoint(sketch, "E34.2.4", {"position": v(47.25, 0) * mm});
            skLineSegment(sketch, "E34.2.5", {"start": v(54.25, -7) * mm, "end": v(42.25, 9) * mm});
            skLineSegment(sketch, "E34.2.6", {"start": v(52.25, 9) * mm, "end": v(52.25, 7) * mm});
            skLineSegment(sketch, "E34.2.7", {"start": v(52.25, 9) * mm, "end": v(40.25, -7) * mm});
            skLineSegment(sketch, "E34.2.8", {"start": v(54.25, 9) * mm, "end": v(52.25, 9) * mm});
            skLineSegment(sketch, "E34.2.9", {"start": v(54.25, 7) * mm, "end": v(52.25, 7) * mm});
            skLineSegment(sketch, "E34.2.10", {"start": v(54.25, 7) * mm, "end": v(42.25, -9) * mm});
            skLineSegment(sketch, "E34.2.11", {"start": v(42.25, 9) * mm, "end": v(42.25, 7) * mm});
            skLineSegment(sketch, "E34.2.12", {"start": v(42.25, -9) * mm, "end": v(42.25, -7) * mm});
            skLineSegment(sketch, "E34.2.13", {"start": v(54.25, -9) * mm, "end": v(54.25, 9) * mm});
            skLineSegment(sketch, "E34.2.14", {"start": v(40.25, 9) * mm, "end": v(42.25, 9) * mm});
            skLineSegment(sketch, "E34.2.15", {"start": v(40.25, -7) * mm, "end": v(42.25, -7) * mm});
            skLineSegment(sketch, "E34.2.16", {"start": v(54.25, -9) * mm, "end": v(40.25, -9) * mm});
            skLineSegment(sketch, "E34.2.17", {"start": v(40.25, 9) * mm, "end": v(40.25, 7) * mm});
            skLineSegment(sketch, "E34.2.18", {"start": v(40.25, 7) * mm, "end": v(42.25, 7) * mm});
            skLineSegment(sketch, "E34.2.19", {"start": v(52.25, -9) * mm, "end": v(52.25, -7) * mm});
            skLineSegment(sketch, "E34.2.20", {"start": v(40.25, -9) * mm, "end": v(40.25, 9) * mm});
            skLineSegment(sketch, "E34.2.21", {"start": v(40.25, -9) * mm, "end": v(40.25, -7) * mm});
            skLineSegment(sketch, "E34.2.22", {"start": v(54.25, -9) * mm, "end": v(52.25, -9) * mm});
            skLineSegment(sketch, "E34.2.23", {"start": v(40.25, -9) * mm, "end": v(42.25, -9) * mm});
            skLineSegment(sketch, "E34.2.24", {"start": v(54.25, -9) * mm, "end": v(54.25, -7) * mm});
            skLineSegment(sketch, "E35.3.3.0", {"start": v(32, 44.72) * mm, "end": v(22.1, 34.83) * mm});
            skLineSegment(sketch, "E35.6.3.0", {"start": v(43.31, 33.41) * mm, "end": v(41.9, 32) * mm});
            skLineSegment(sketch, "E35.9.3.0", {"start": v(23.51, 33.41) * mm, "end": v(43.31, 30.58) * mm});
            skPoint(sketch, "E35.12.3.0", {"position": v(33.41, 33.41) * mm});
            skLineSegment(sketch, "E35.13.3.0", {"start": v(43.31, 33.41) * mm, "end": v(23.51, 36.24) * mm});
            skLineSegment(sketch, "E35.16.3.0", {"start": v(30.58, 43.31) * mm, "end": v(32, 41.9) * mm});
            skLineSegment(sketch, "E35.19.3.0", {"start": v(30.58, 43.31) * mm, "end": v(33.41, 23.51) * mm});
            skLineSegment(sketch, "E35.22.3.0", {"start": v(32, 44.72) * mm, "end": v(30.58, 43.31) * mm});
            skLineSegment(sketch, "E35.25.3.0", {"start": v(33.41, 43.31) * mm, "end": v(32, 41.9) * mm});
            skLineSegment(sketch, "E35.28.3.0", {"start": v(33.41, 43.31) * mm, "end": v(36.24, 23.51) * mm});
            skLineSegment(sketch, "E35.31.3.0", {"start": v(23.51, 36.24) * mm, "end": v(24.93, 34.83) * mm});
            skLineSegment(sketch, "E35.34.3.0", {"start": v(36.24, 23.51) * mm, "end": v(34.83, 24.93) * mm});
            skLineSegment(sketch, "E35.37.3.0", {"start": v(44.72, 32) * mm, "end": v(32, 44.72) * mm});
            skLineSegment(sketch, "E35.38.3.0", {"start": v(32, 44.72) * mm, "end": v(33.41, 43.31) * mm});
            skLineSegment(sketch, "E35.40.3.0", {"start": v(22.1, 34.83) * mm, "end": v(23.51, 36.24) * mm});
            skLineSegment(sketch, "E35.43.3.0", {"start": v(33.41, 23.51) * mm, "end": v(34.83, 24.93) * mm});
            skLineSegment(sketch, "E35.46.3.0", {"start": v(44.72, 32) * mm, "end": v(34.83, 22.1) * mm});
            skLineSegment(sketch, "E35.49.3.0", {"start": v(22.1, 34.83) * mm, "end": v(23.51, 33.41) * mm});
            skLineSegment(sketch, "E35.52.3.0", {"start": v(23.51, 33.41) * mm, "end": v(24.93, 34.83) * mm});
            skLineSegment(sketch, "E35.55.3.0", {"start": v(43.31, 30.58) * mm, "end": v(41.9, 32) * mm});
            skLineSegment(sketch, "E35.58.3.0", {"start": v(34.83, 22.1) * mm, "end": v(22.1, 34.83) * mm});
            skLineSegment(sketch, "E35.61.3.0", {"start": v(34.83, 22.1) * mm, "end": v(33.41, 23.51) * mm});
            skLineSegment(sketch, "E35.64.3.0", {"start": v(44.72, 32) * mm, "end": v(43.31, 30.58) * mm});
            skLineSegment(sketch, "E35.67.3.0", {"start": v(34.83, 22.1) * mm, "end": v(36.24, 23.51) * mm});
            skLineSegment(sketch, "E35.70.3.0", {"start": v(44.72, 32) * mm, "end": v(43.31, 33.41) * mm});
            skLineSegment(sketch, "E35.3.4.0", {"start": v(-9, 54.25) * mm, "end": v(-9, 40.25) * mm});
            skLineSegment(sketch, "E35.6.4.0", {"start": v(7, 54.25) * mm, "end": v(7, 52.25) * mm});
            skLineSegment(sketch, "E35.9.4.0", {"start": v(-7, 40.25) * mm, "end": v(9, 52.25) * mm});
            skPoint(sketch, "E35.12.4.0", {"position": v(0, 47.25) * mm});
            skLineSegment(sketch, "E35.13.4.0", {"start": v(7, 54.25) * mm, "end": v(-9, 42.25) * mm});
            skLineSegment(sketch, "E35.16.4.0", {"start": v(-9, 52.25) * mm, "end": v(-7, 52.25) * mm});
            skLineSegment(sketch, "E35.19.4.0", {"start": v(-9, 52.25) * mm, "end": v(7, 40.25) * mm});
            skLineSegment(sketch, "E35.22.4.0", {"start": v(-9, 54.25) * mm, "end": v(-9, 52.25) * mm});
            skLineSegment(sketch, "E35.25.4.0", {"start": v(-7, 54.25) * mm, "end": v(-7, 52.25) * mm});
            skLineSegment(sketch, "E35.28.4.0", {"start": v(-7, 54.25) * mm, "end": v(9, 42.25) * mm});
            skLineSegment(sketch, "E35.31.4.0", {"start": v(-9, 42.25) * mm, "end": v(-7, 42.25) * mm});
            skLineSegment(sketch, "E35.34.4.0", {"start": v(9, 42.25) * mm, "end": v(7, 42.25) * mm});
            skLineSegment(sketch, "E35.37.4.0", {"start": v(9, 54.25) * mm, "end": v(-9, 54.25) * mm});
            skLineSegment(sketch, "E35.38.4.0", {"start": v(-9, 54.25) * mm, "end": v(-7, 54.25) * mm});
            skLineSegment(sketch, "E35.40.4.0", {"start": v(-9, 40.25) * mm, "end": v(-9, 42.25) * mm});
            skLineSegment(sketch, "E35.43.4.0", {"start": v(7, 40.25) * mm, "end": v(7, 42.25) * mm});
            skLineSegment(sketch, "E35.46.4.0", {"start": v(9, 54.25) * mm, "end": v(9, 40.25) * mm});
            skLineSegment(sketch, "E35.49.4.0", {"start": v(-9, 40.25) * mm, "end": v(-7, 40.25) * mm});
            skLineSegment(sketch, "E35.52.4.0", {"start": v(-7, 40.25) * mm, "end": v(-7, 42.25) * mm});
            skLineSegment(sketch, "E35.55.4.0", {"start": v(9, 52.25) * mm, "end": v(7, 52.25) * mm});
            skLineSegment(sketch, "E35.58.4.0", {"start": v(9, 40.25) * mm, "end": v(-9, 40.25) * mm});
            skLineSegment(sketch, "E35.61.4.0", {"start": v(9, 40.25) * mm, "end": v(7, 40.25) * mm});
            skLineSegment(sketch, "E35.64.4.0", {"start": v(9, 54.25) * mm, "end": v(9, 52.25) * mm});
            skLineSegment(sketch, "E35.67.4.0", {"start": v(9, 40.25) * mm, "end": v(9, 42.25) * mm});
            skLineSegment(sketch, "E35.70.4.0", {"start": v(9, 54.25) * mm, "end": v(7, 54.25) * mm});
            skLineSegment(sketch, "E35.3.5.0", {"start": v(-44.72, 32) * mm, "end": v(-34.83, 22.1) * mm});
            skLineSegment(sketch, "E35.6.5.0", {"start": v(-33.41, 43.31) * mm, "end": v(-32, 41.9) * mm});
            skLineSegment(sketch, "E35.9.5.0", {"start": v(-33.41, 23.51) * mm, "end": v(-30.58, 43.31) * mm});
            skPoint(sketch, "E35.12.5.0", {"position": v(-33.41, 33.41) * mm});
            skLineSegment(sketch, "E35.13.5.0", {"start": v(-33.41, 43.31) * mm, "end": v(-36.24, 23.51) * mm});
            skLineSegment(sketch, "E35.16.5.0", {"start": v(-43.31, 30.58) * mm, "end": v(-41.9, 32) * mm});
            skLineSegment(sketch, "E35.19.5.0", {"start": v(-43.31, 30.58) * mm, "end": v(-23.51, 33.41) * mm});
            skLineSegment(sketch, "E35.22.5.0", {"start": v(-44.72, 32) * mm, "end": v(-43.31, 30.58) * mm});
            skLineSegment(sketch, "E35.25.5.0", {"start": v(-43.31, 33.41) * mm, "end": v(-41.9, 32) * mm});
            skLineSegment(sketch, "E35.28.5.0", {"start": v(-43.31, 33.41) * mm, "end": v(-23.51, 36.24) * mm});
            skLineSegment(sketch, "E35.31.5.0", {"start": v(-36.24, 23.51) * mm, "end": v(-34.83, 24.93) * mm});
            skLineSegment(sketch, "E35.34.5.0", {"start": v(-23.51, 36.24) * mm, "end": v(-24.93, 34.83) * mm});
            skLineSegment(sketch, "E35.37.5.0", {"start": v(-32, 44.72) * mm, "end": v(-44.72, 32) * mm});
            skLineSegment(sketch, "E35.38.5.0", {"start": v(-44.72, 32) * mm, "end": v(-43.31, 33.41) * mm});
            skLineSegment(sketch, "E35.40.5.0", {"start": v(-34.83, 22.1) * mm, "end": v(-36.24, 23.51) * mm});
            skLineSegment(sketch, "E35.43.5.0", {"start": v(-23.51, 33.41) * mm, "end": v(-24.93, 34.83) * mm});
            skLineSegment(sketch, "E35.46.5.0", {"start": v(-32, 44.72) * mm, "end": v(-22.1, 34.83) * mm});
            skLineSegment(sketch, "E35.49.5.0", {"start": v(-34.83, 22.1) * mm, "end": v(-33.41, 23.51) * mm});
            skLineSegment(sketch, "E35.52.5.0", {"start": v(-33.41, 23.51) * mm, "end": v(-34.83, 24.93) * mm});
            skLineSegment(sketch, "E35.55.5.0", {"start": v(-30.58, 43.31) * mm, "end": v(-32, 41.9) * mm});
            skLineSegment(sketch, "E35.58.5.0", {"start": v(-22.1, 34.83) * mm, "end": v(-34.83, 22.1) * mm});
            skLineSegment(sketch, "E35.61.5.0", {"start": v(-22.1, 34.83) * mm, "end": v(-23.51, 33.41) * mm});
            skLineSegment(sketch, "E35.64.5.0", {"start": v(-32, 44.72) * mm, "end": v(-30.58, 43.31) * mm});
            skLineSegment(sketch, "E35.67.5.0", {"start": v(-22.1, 34.83) * mm, "end": v(-23.51, 36.24) * mm});
            skLineSegment(sketch, "E35.70.5.0", {"start": v(-32, 44.72) * mm, "end": v(-33.41, 43.31) * mm});
            skLineSegment(sketch, "E35.3.6.0", {"start": v(-54.25, -9) * mm, "end": v(-40.25, -9) * mm});
            skLineSegment(sketch, "E35.6.6.0", {"start": v(-54.25, 7) * mm, "end": v(-52.25, 7) * mm});
            skLineSegment(sketch, "E35.9.6.0", {"start": v(-40.25, -7) * mm, "end": v(-52.25, 9) * mm});
            skPoint(sketch, "E35.12.6.0", {"position": v(-47.25, 0) * mm});
            skLineSegment(sketch, "E35.13.6.0", {"start": v(-54.25, 7) * mm, "end": v(-42.25, -9) * mm});
            skLineSegment(sketch, "E35.16.6.0", {"start": v(-52.25, -9) * mm, "end": v(-52.25, -7) * mm});
            skLineSegment(sketch, "E35.19.6.0", {"start": v(-52.25, -9) * mm, "end": v(-40.25, 7) * mm});
            skLineSegment(sketch, "E35.22.6.0", {"start": v(-54.25, -9) * mm, "end": v(-52.25, -9) * mm});
            skLineSegment(sketch, "E35.25.6.0", {"start": v(-54.25, -7) * mm, "end": v(-52.25, -7) * mm});
            skLineSegment(sketch, "E35.28.6.0", {"start": v(-54.25, -7) * mm, "end": v(-42.25, 9) * mm});
            skLineSegment(sketch, "E35.31.6.0", {"start": v(-42.25, -9) * mm, "end": v(-42.25, -7) * mm});
            skLineSegment(sketch, "E35.34.6.0", {"start": v(-42.25, 9) * mm, "end": v(-42.25, 7) * mm});
            skLineSegment(sketch, "E35.37.6.0", {"start": v(-54.25, 9) * mm, "end": v(-54.25, -9) * mm});
            skLineSegment(sketch, "E35.38.6.0", {"start": v(-54.25, -9) * mm, "end": v(-54.25, -7) * mm});
            skLineSegment(sketch, "E35.40.6.0", {"start": v(-40.25, -9) * mm, "end": v(-42.25, -9) * mm});
            skLineSegment(sketch, "E35.43.6.0", {"start": v(-40.25, 7) * mm, "end": v(-42.25, 7) * mm});
            skLineSegment(sketch, "E35.46.6.0", {"start": v(-54.25, 9) * mm, "end": v(-40.25, 9) * mm});
            skLineSegment(sketch, "E35.49.6.0", {"start": v(-40.25, -9) * mm, "end": v(-40.25, -7) * mm});
            skLineSegment(sketch, "E35.52.6.0", {"start": v(-40.25, -7) * mm, "end": v(-42.25, -7) * mm});
            skLineSegment(sketch, "E35.55.6.0", {"start": v(-52.25, 9) * mm, "end": v(-52.25, 7) * mm});
            skLineSegment(sketch, "E35.58.6.0", {"start": v(-40.25, 9) * mm, "end": v(-40.25, -9) * mm});
            skLineSegment(sketch, "E35.61.6.0", {"start": v(-40.25, 9) * mm, "end": v(-40.25, 7) * mm});
            skLineSegment(sketch, "E35.64.6.0", {"start": v(-54.25, 9) * mm, "end": v(-52.25, 9) * mm});
            skLineSegment(sketch, "E35.67.6.0", {"start": v(-40.25, 9) * mm, "end": v(-42.25, 9) * mm});
            skLineSegment(sketch, "E35.70.6.0", {"start": v(-54.25, 9) * mm, "end": v(-54.25, 7) * mm});
            skLineSegment(sketch, "E35.3.7.0", {"start": v(-32, -44.72) * mm, "end": v(-22.1, -34.83) * mm});
            skLineSegment(sketch, "E35.6.7.0", {"start": v(-43.31, -33.41) * mm, "end": v(-41.9, -32) * mm});
            skLineSegment(sketch, "E35.9.7.0", {"start": v(-23.51, -33.41) * mm, "end": v(-43.31, -30.58) * mm});
            skPoint(sketch, "E35.12.7.0", {"position": v(-33.41, -33.41) * mm});
            skLineSegment(sketch, "E35.13.7.0", {"start": v(-43.31, -33.41) * mm, "end": v(-23.51, -36.24) * mm});
            skLineSegment(sketch, "E35.16.7.0", {"start": v(-30.58, -43.31) * mm, "end": v(-32, -41.9) * mm});
            skLineSegment(sketch, "E35.19.7.0", {"start": v(-30.58, -43.31) * mm, "end": v(-33.41, -23.51) * mm});
            skLineSegment(sketch, "E35.22.7.0", {"start": v(-32, -44.72) * mm, "end": v(-30.58, -43.31) * mm});
            skLineSegment(sketch, "E35.25.7.0", {"start": v(-33.41, -43.31) * mm, "end": v(-32, -41.9) * mm});
            skLineSegment(sketch, "E35.28.7.0", {"start": v(-33.41, -43.31) * mm, "end": v(-36.24, -23.51) * mm});
            skLineSegment(sketch, "E35.31.7.0", {"start": v(-23.51, -36.24) * mm, "end": v(-24.93, -34.83) * mm});
            skLineSegment(sketch, "E35.34.7.0", {"start": v(-36.24, -23.51) * mm, "end": v(-34.83, -24.93) * mm});
            skLineSegment(sketch, "E35.37.7.0", {"start": v(-44.72, -32) * mm, "end": v(-32, -44.72) * mm});
            skLineSegment(sketch, "E35.38.7.0", {"start": v(-32, -44.72) * mm, "end": v(-33.41, -43.31) * mm});
            skLineSegment(sketch, "E35.40.7.0", {"start": v(-22.1, -34.83) * mm, "end": v(-23.51, -36.24) * mm});
            skLineSegment(sketch, "E35.43.7.0", {"start": v(-33.41, -23.51) * mm, "end": v(-34.83, -24.93) * mm});
            skLineSegment(sketch, "E35.46.7.0", {"start": v(-44.72, -32) * mm, "end": v(-34.83, -22.1) * mm});
            skLineSegment(sketch, "E35.49.7.0", {"start": v(-22.1, -34.83) * mm, "end": v(-23.51, -33.41) * mm});
            skLineSegment(sketch, "E35.52.7.0", {"start": v(-23.51, -33.41) * mm, "end": v(-24.93, -34.83) * mm});
            skLineSegment(sketch, "E35.55.7.0", {"start": v(-43.31, -30.58) * mm, "end": v(-41.9, -32) * mm});
            skLineSegment(sketch, "E35.58.7.0", {"start": v(-34.83, -22.1) * mm, "end": v(-22.1, -34.83) * mm});
            skLineSegment(sketch, "E35.61.7.0", {"start": v(-34.83, -22.1) * mm, "end": v(-33.41, -23.51) * mm});
            skLineSegment(sketch, "E35.64.7.0", {"start": v(-44.72, -32) * mm, "end": v(-43.31, -30.58) * mm});
            skLineSegment(sketch, "E35.67.7.0", {"start": v(-34.83, -22.1) * mm, "end": v(-36.24, -23.51) * mm});
            skLineSegment(sketch, "E35.70.7.0", {"start": v(-44.72, -32) * mm, "end": v(-43.31, -33.41) * mm});
            skSolve(sketch);
        }
        {
            var Q0;
            Q0=makeQuery(id+"F4.imprint","IMPRINT",FACE,{"disambiguationData":[TD([[makeQuery(id+"F4.imprint","IMPRINT",EDGE,{"derivedFrom":sQuery(id+"F4.wireOp",EDGE,"E20.bottom")}),-1.0]])]});
            var Q1;
            {var subQ0=sQuery(id+"F4.wireOp",EDGE,"E18.bottom");Q1=makeQuery(id+"F4.imprint","IMPRINT",FACE,{"disambiguationData":[TD([[makeQuery(id+"F4.imprint","IMPRINT",EDGE,{"derivedFrom":subQ0}),1.0]])]});}
            var Q2;
            {var subQ0=sQuery(id+"F4.wireOp",EDGE,"E17.top");Q2=makeQuery(id+"F4.imprint","IMPRINT",FACE,{"disambiguationData":[TD([[makeQuery(id+"F4.imprint","IMPRINT",EDGE,{"derivedFrom":subQ0}),1.0]])]});}
            var Q3;
            {var subQ0=sQuery(id+"F4.wireOp",EDGE,"E19.bottom");Q3=makeQuery(id+"F4.imprint","IMPRINT",FACE,{"disambiguationData":[TD([[makeQuery(id+"F4.imprint","IMPRINT",EDGE,{"derivedFrom":subQ0}),-1.0]])]});}
            var Q4;
            Q4=makeQuery(id+"F4.imprint","IMPRINT",FACE,{"disambiguationData":[TD([[makeQuery(id+"F4.imprint","IMPRINT",EDGE,{"derivedFrom":sQuery(id+"F4.wireOp",EDGE,"E19.top")}),-1.0]])]});
            var Q5;
            Q5=makeQuery(id+"F4.imprint","IMPRINT",FACE,{"disambiguationData":[TD([[makeQuery(id+"F4.imprint","IMPRINT",EDGE,{"derivedFrom":sQuery(id+"F4.wireOp",EDGE,"E22.1.2")}),1.0]])]});
            var Q6;
            {var subQ0=sQuery(id+"F4.wireOp",EDGE,"E22.1.8");Q6=makeQuery(id+"F4.imprint","IMPRINT",FACE,{"disambiguationData":[TD([[makeQuery(id+"F4.imprint","IMPRINT",EDGE,{"derivedFrom":subQ0}),-1.0]])]});}
            var Q7;
            {var subQ0=sQuery(id+"F4.wireOp",EDGE,"E22.1.9");Q7=makeQuery(id+"F4.imprint","IMPRINT",FACE,{"disambiguationData":[TD([[makeQuery(id+"F4.imprint","IMPRINT",EDGE,{"derivedFrom":subQ0}),1.0]])]});}
            var Q8;
            Q8=makeQuery(id+"F4.imprint","IMPRINT",FACE,{"disambiguationData":[TD([[makeQuery(id+"F4.imprint","IMPRINT",EDGE,{"derivedFrom":sQuery(id+"F4.wireOp",EDGE,"E22.1.0")}),1.0]])]});
            var Q9;
            {var subQ0=sQuery(id+"F4.wireOp",EDGE,"E22.1.7");Q9=makeQuery(id+"F4.imprint","IMPRINT",FACE,{"disambiguationData":[TD([[makeQuery(id+"F4.imprint","IMPRINT",EDGE,{"derivedFrom":subQ0}),1.0]])]});}
            var Q10;
            {var subQ0=sQuery(id+"F4.wireOp",EDGE,"E22.2.8");Q10=makeQuery(id+"F4.imprint","IMPRINT",FACE,{"disambiguationData":[TD([[makeQuery(id+"F4.imprint","IMPRINT",EDGE,{"derivedFrom":subQ0}),-1.0]])]});}
            var Q11;
            {var subQ0=sQuery(id+"F4.wireOp",EDGE,"E22.2.9");Q11=makeQuery(id+"F4.imprint","IMPRINT",FACE,{"disambiguationData":[TD([[makeQuery(id+"F4.imprint","IMPRINT",EDGE,{"derivedFrom":subQ0}),1.0]])]});}
            var Q12;
            Q12=makeQuery(id+"F4.imprint","IMPRINT",FACE,{"disambiguationData":[TD([[makeQuery(id+"F4.imprint","IMPRINT",EDGE,{"derivedFrom":sQuery(id+"F4.wireOp",EDGE,"E22.2.2")}),1.0]])]});
            var Q13;
            Q13=makeQuery(id+"F4.imprint","IMPRINT",FACE,{"disambiguationData":[TD([[makeQuery(id+"F4.imprint","IMPRINT",EDGE,{"derivedFrom":sQuery(id+"F4.wireOp",EDGE,"E22.2.0")}),1.0]])]});
            var Q14;
            {var subQ0=sQuery(id+"F4.wireOp",EDGE,"E22.2.7");Q14=makeQuery(id+"F4.imprint","IMPRINT",FACE,{"disambiguationData":[TD([[makeQuery(id+"F4.imprint","IMPRINT",EDGE,{"derivedFrom":subQ0}),1.0]])]});}
            var Q15;
            Q15=makeQuery(id+"F4.imprint","IMPRINT",FACE,{"disambiguationData":[TD([[makeQuery(id+"F4.imprint","IMPRINT",EDGE,{"derivedFrom":sQuery(id+"F4.wireOp",EDGE,"E23.6.3.0")}),1.0]])]});
            var Q16;
            {var subQ0=sQuery(id+"F4.wireOp",EDGE,"E23.22.3.0");Q16=makeQuery(id+"F4.imprint","IMPRINT",FACE,{"disambiguationData":[TD([[makeQuery(id+"F4.imprint","IMPRINT",EDGE,{"derivedFrom":subQ0}),-1.0]])]});}
            var Q17;
            {var subQ0=sQuery(id+"F4.wireOp",EDGE,"E23.25.3.0");Q17=makeQuery(id+"F4.imprint","IMPRINT",FACE,{"disambiguationData":[TD([[makeQuery(id+"F4.imprint","IMPRINT",EDGE,{"derivedFrom":subQ0}),1.0]])]});}
            var Q18;
            Q18=makeQuery(id+"F4.imprint","IMPRINT",FACE,{"disambiguationData":[TD([[makeQuery(id+"F4.imprint","IMPRINT",EDGE,{"derivedFrom":sQuery(id+"F4.wireOp",EDGE,"E23.9.3.0")}),1.0]])]});
            var Q19;
            {var subQ0=sQuery(id+"F4.wireOp",EDGE,"E23.19.3.0");Q19=makeQuery(id+"F4.imprint","IMPRINT",FACE,{"disambiguationData":[TD([[makeQuery(id+"F4.imprint","IMPRINT",EDGE,{"derivedFrom":subQ0}),1.0]])]});}
            var Q20;
            Q20=makeQuery(id+"F4.imprint","IMPRINT",FACE,{"disambiguationData":[TD([[makeQuery(id+"F4.imprint","IMPRINT",EDGE,{"derivedFrom":sQuery(id+"F4.wireOp",EDGE,"E23.6.4.0")}),1.0]])]});
            var Q21;
            {var subQ0=sQuery(id+"F4.wireOp",EDGE,"E23.22.4.0");Q21=makeQuery(id+"F4.imprint","IMPRINT",FACE,{"disambiguationData":[TD([[makeQuery(id+"F4.imprint","IMPRINT",EDGE,{"derivedFrom":subQ0}),-1.0]])]});}
            var Q22;
            {var subQ0=sQuery(id+"F4.wireOp",EDGE,"E23.25.4.0");Q22=makeQuery(id+"F4.imprint","IMPRINT",FACE,{"disambiguationData":[TD([[makeQuery(id+"F4.imprint","IMPRINT",EDGE,{"derivedFrom":subQ0}),1.0]])]});}
            var Q23;
            Q23=makeQuery(id+"F4.imprint","IMPRINT",FACE,{"disambiguationData":[TD([[makeQuery(id+"F4.imprint","IMPRINT",EDGE,{"derivedFrom":sQuery(id+"F4.wireOp",EDGE,"E23.6.5.0")}),1.0]])]});
            var Q24;
            {var subQ0=sQuery(id+"F4.wireOp",EDGE,"E23.22.5.0");Q24=makeQuery(id+"F4.imprint","IMPRINT",FACE,{"disambiguationData":[TD([[makeQuery(id+"F4.imprint","IMPRINT",EDGE,{"derivedFrom":subQ0}),-1.0]])]});}
            var Q25;
            {var subQ0=sQuery(id+"F4.wireOp",EDGE,"E23.25.5.0");Q25=makeQuery(id+"F4.imprint","IMPRINT",FACE,{"disambiguationData":[TD([[makeQuery(id+"F4.imprint","IMPRINT",EDGE,{"derivedFrom":subQ0}),1.0]])]});}
            var Q26;
            {var subQ0=sQuery(id+"F4.wireOp",EDGE,"E23.19.5.0");Q26=makeQuery(id+"F4.imprint","IMPRINT",FACE,{"disambiguationData":[TD([[makeQuery(id+"F4.imprint","IMPRINT",EDGE,{"derivedFrom":subQ0}),1.0]])]});}
            var Q27;
            Q27=makeQuery(id+"F4.imprint","IMPRINT",FACE,{"disambiguationData":[TD([[makeQuery(id+"F4.imprint","IMPRINT",EDGE,{"derivedFrom":sQuery(id+"F4.wireOp",EDGE,"E23.9.5.0")}),1.0]])]});
            var Q28;
            {var subQ0=sQuery(id+"F4.wireOp",EDGE,"E23.19.4.0");Q28=makeQuery(id+"F4.imprint","IMPRINT",FACE,{"disambiguationData":[TD([[makeQuery(id+"F4.imprint","IMPRINT",EDGE,{"derivedFrom":subQ0}),1.0]])]});}
            var Q29;
            Q29=makeQuery(id+"F4.imprint","IMPRINT",FACE,{"disambiguationData":[TD([[makeQuery(id+"F4.imprint","IMPRINT",EDGE,{"derivedFrom":sQuery(id+"F4.wireOp",EDGE,"E23.9.4.0")}),1.0]])]});
            var Q30;
            {var subQ0=sQuery(id+"F4.wireOp",EDGE,"E23.22.6.0");Q30=makeQuery(id+"F4.imprint","IMPRINT",FACE,{"disambiguationData":[TD([[makeQuery(id+"F4.imprint","IMPRINT",EDGE,{"derivedFrom":subQ0}),-1.0]])]});}
            var Q31;
            {var subQ0=sQuery(id+"F4.wireOp",EDGE,"E23.25.6.0");Q31=makeQuery(id+"F4.imprint","IMPRINT",FACE,{"disambiguationData":[TD([[makeQuery(id+"F4.imprint","IMPRINT",EDGE,{"derivedFrom":subQ0}),1.0]])]});}
            var Q32;
            Q32=makeQuery(id+"F4.imprint","IMPRINT",FACE,{"disambiguationData":[TD([[makeQuery(id+"F4.imprint","IMPRINT",EDGE,{"derivedFrom":sQuery(id+"F4.wireOp",EDGE,"E23.6.6.0")}),1.0]])]});
            var Q33;
            {var subQ0=sQuery(id+"F4.wireOp",EDGE,"E23.19.6.0");Q33=makeQuery(id+"F4.imprint","IMPRINT",FACE,{"disambiguationData":[TD([[makeQuery(id+"F4.imprint","IMPRINT",EDGE,{"derivedFrom":subQ0}),1.0]])]});}
            var Q34;
            Q34=makeQuery(id+"F4.imprint","IMPRINT",FACE,{"disambiguationData":[TD([[makeQuery(id+"F4.imprint","IMPRINT",EDGE,{"derivedFrom":sQuery(id+"F4.wireOp",EDGE,"E23.9.6.0")}),1.0]])]});
            var Q35;
            Q35=makeQuery(id+"F4.imprint","IMPRINT",FACE,{"disambiguationData":[TD([[makeQuery(id+"F4.imprint","IMPRINT",EDGE,{"derivedFrom":sQuery(id+"F4.wireOp",EDGE,"E23.6.7.0")}),1.0]])]});
            var Q36;
            {var subQ0=sQuery(id+"F4.wireOp",EDGE,"E23.22.7.0");Q36=makeQuery(id+"F4.imprint","IMPRINT",FACE,{"disambiguationData":[TD([[makeQuery(id+"F4.imprint","IMPRINT",EDGE,{"derivedFrom":subQ0}),-1.0]])]});}
            var Q37;
            {var subQ0=sQuery(id+"F4.wireOp",EDGE,"E23.19.7.0");Q37=makeQuery(id+"F4.imprint","IMPRINT",FACE,{"disambiguationData":[TD([[makeQuery(id+"F4.imprint","IMPRINT",EDGE,{"derivedFrom":subQ0}),1.0]])]});}
            var Q38;
            Q38=makeQuery(id+"F4.imprint","IMPRINT",FACE,{"disambiguationData":[TD([[makeQuery(id+"F4.imprint","IMPRINT",EDGE,{"derivedFrom":sQuery(id+"F4.wireOp",EDGE,"E23.9.7.0")}),1.0]])]});
            var Q39;
            {var subQ0=sQuery(id+"F4.wireOp",EDGE,"E23.25.7.0");Q39=makeQuery(id+"F4.imprint","IMPRINT",FACE,{"disambiguationData":[TD([[makeQuery(id+"F4.imprint","IMPRINT",EDGE,{"derivedFrom":subQ0}),1.0]])]});}
            extrude(context, id + "F5", {"entities" : qUnion([Q0, Q1, Q2, Q3, Q4, Q5, Q6, Q7, Q8, Q9, Q10, Q11, Q12, Q13, Q14, Q15, Q16, Q17, Q18, Q19, Q20, Q21, Q22, Q23, Q24, Q25, Q26, Q27, Q28, Q29, Q30, Q31, Q32, Q33, Q34, Q35, Q36, Q37, Q38, Q39]), "operationType" : NewBodyOperationType.ADD, "depth" : 5 * mm, "offsetDistance" : 25 * mm, "hasSecondDirection" : true, "secondDirectionOppositeDirection" : true, "secondDirectionDepth" : 2 * mm});
        }
        {
            var Q0;
            Q0=makeQuery(id+"F5.opExtrude","CAP_EDGE",EDGE,{"disambiguationData":[OSD([sQuery(id+"F4.wireOp",EDGE,"E22.2.15")])],"isStart":false});
            var Q1;
            Q1=makeQuery(id+"F5.opExtrude","CAP_EDGE",EDGE,{"disambiguationData":[OSD([sQuery(id+"F4.wireOp",EDGE,"E22.2.13")])],"isStart":false});
            var Q2;
            Q2=makeQuery(id+"F5.opExtrude","CAP_EDGE",EDGE,{"disambiguationData":[OSD([sQuery(id+"F4.wireOp",EDGE,"E23.43.3.0")])],"isStart":false});
            var Q3;
            Q3=makeQuery(id+"F5.opExtrude","CAP_EDGE",EDGE,{"disambiguationData":[OSD([sQuery(id+"F4.wireOp",EDGE,"E22.1.13")])],"isStart":false});
            var Q4;
            Q4=makeQuery(id+"F5.opExtrude","CAP_EDGE",EDGE,{"disambiguationData":[OSD([sQuery(id+"F4.wireOp",EDGE,"E23.37.3.0")])],"isStart":false});
            var Q5;
            Q5=makeQuery(id+"F5.opExtrude","CAP_EDGE",EDGE,{"disambiguationData":[OSD([sQuery(id+"F4.wireOp",EDGE,"E23.43.4.0")])],"isStart":false});
            var Q6;
            Q6=makeQuery(id+"F5.opExtrude","CAP_EDGE",EDGE,{"disambiguationData":[OSD([sQuery(id+"F4.wireOp",EDGE,"E23.37.4.0")])],"isStart":false});
            var Q7;
            Q7=makeQuery(id+"F5.opExtrude","CAP_EDGE",EDGE,{"disambiguationData":[OSD([sQuery(id+"F4.wireOp",EDGE,"E23.43.5.0")])],"isStart":false});
            var Q8;
            Q8=makeQuery(id+"F5.opExtrude","CAP_EDGE",EDGE,{"disambiguationData":[OSD([sQuery(id+"F4.wireOp",EDGE,"E23.37.5.0")])],"isStart":false});
            var Q9;
            Q9=makeQuery(id+"F5.opExtrude","CAP_EDGE",EDGE,{"disambiguationData":[OSD([sQuery(id+"F4.wireOp",EDGE,"E23.43.6.0")])],"isStart":false});
            var Q10;
            Q10=makeQuery(id+"F5.opExtrude","CAP_EDGE",EDGE,{"disambiguationData":[OSD([sQuery(id+"F4.wireOp",EDGE,"E23.37.6.0")])],"isStart":false});
            var Q11;
            Q11=makeQuery(id+"F5.opExtrude","CAP_EDGE",EDGE,{"disambiguationData":[OSD([sQuery(id+"F4.wireOp",EDGE,"E23.43.7.0")])],"isStart":false});
            var Q12;
            Q12=makeQuery(id+"F5.opExtrude","CAP_EDGE",EDGE,{"disambiguationData":[OSD([sQuery(id+"F4.wireOp",EDGE,"E23.37.7.0")])],"isStart":false});
            var Q13;
            Q13=makeQuery(id+"F5.opExtrude","CAP_EDGE",EDGE,{"disambiguationData":[OSD([sQuery(id+"F4.wireOp",EDGE,"E21.left")])],"isStart":false});
            var Q14;
            Q14=makeQuery(id+"F5.opExtrude","CAP_EDGE",EDGE,{"disambiguationData":[OSD([sQuery(id+"F4.wireOp",EDGE,"E20.right")])],"isStart":false});
            var Q15;
            Q15=makeQuery(id+"F5.opExtrude","CAP_EDGE",EDGE,{"disambiguationData":[OSD([sQuery(id+"F4.wireOp",EDGE,"E22.1.15")])],"isStart":false});
            var Q16;
            Q16=makeQuery(id+"F3.opExtrude","CAP_EDGE",EDGE,{"disambiguationData":[OSD([sQuery(id+"F0.wireOp",EDGE,"E14.right")])],"isStart":false});
            var Q17;
            Q17=makeQuery(id+"F3.opExtrude","CAP_EDGE",EDGE,{"disambiguationData":[OSD([sQuery(id+"F0.wireOp",EDGE,"E15.1.1")])],"isStart":false});
            var Q18;
            Q18=makeQuery(id+"F3.opExtrude","CAP_EDGE",EDGE,{"disambiguationData":[OSD([sQuery(id+"F0.wireOp",EDGE,"E15.1.3")])],"isStart":false});
            var Q19;
            Q19=makeQuery(id+"F3.opExtrude","CAP_EDGE",EDGE,{"disambiguationData":[OSD([sQuery(id+"F0.wireOp",EDGE,"E15.2.1")])],"isStart":false});
            var Q20;
            Q20=makeQuery(id+"F3.opExtrude","CAP_EDGE",EDGE,{"disambiguationData":[OSD([sQuery(id+"F0.wireOp",EDGE,"E15.2.3")])],"isStart":false});
            var Q21;
            Q21=makeQuery(id+"F3.opExtrude","CAP_EDGE",EDGE,{"disambiguationData":[OSD([sQuery(id+"F0.wireOp",EDGE,"E16.3.3.0")])],"isStart":false});
            var Q22;
            Q22=makeQuery(id+"F3.opExtrude","CAP_EDGE",EDGE,{"disambiguationData":[OSD([sQuery(id+"F0.wireOp",EDGE,"E16.9.3.0")])],"isStart":false});
            var Q23;
            Q23=makeQuery(id+"F3.opExtrude","CAP_EDGE",EDGE,{"disambiguationData":[OSD([sQuery(id+"F0.wireOp",EDGE,"E16.3.4.0")])],"isStart":false});
            var Q24;
            Q24=makeQuery(id+"F3.opExtrude","CAP_EDGE",EDGE,{"disambiguationData":[OSD([sQuery(id+"F0.wireOp",EDGE,"E16.9.4.0")])],"isStart":false});
            var Q25;
            Q25=makeQuery(id+"F3.opExtrude","CAP_EDGE",EDGE,{"disambiguationData":[OSD([sQuery(id+"F0.wireOp",EDGE,"E16.3.5.0")])],"isStart":false});
            var Q26;
            Q26=makeQuery(id+"F3.opExtrude","CAP_EDGE",EDGE,{"disambiguationData":[OSD([sQuery(id+"F0.wireOp",EDGE,"E16.9.5.0")])],"isStart":false});
            var Q27;
            Q27=makeQuery(id+"F3.opExtrude","CAP_EDGE",EDGE,{"disambiguationData":[OSD([sQuery(id+"F0.wireOp",EDGE,"E16.3.6.0")])],"isStart":false});
            var Q28;
            Q28=makeQuery(id+"F3.opExtrude","CAP_EDGE",EDGE,{"disambiguationData":[OSD([sQuery(id+"F0.wireOp",EDGE,"E16.9.6.0")])],"isStart":false});
            var Q29;
            Q29=makeQuery(id+"F3.opExtrude","CAP_EDGE",EDGE,{"disambiguationData":[OSD([sQuery(id+"F0.wireOp",EDGE,"E16.3.7.0")])],"isStart":false});
            var Q30;
            Q30=makeQuery(id+"F3.opExtrude","CAP_EDGE",EDGE,{"disambiguationData":[OSD([sQuery(id+"F0.wireOp",EDGE,"E16.9.7.0")])],"isStart":false});
            var Q31;
            Q31=makeQuery(id+"F3.opExtrude","CAP_EDGE",EDGE,{"disambiguationData":[OSD([sQuery(id+"F0.wireOp",EDGE,"E14.left")])],"isStart":false});
            chamfer(context, id + "F6", {"entities" : qUnion([Q0, Q1, Q2, Q3, Q4, Q5, Q6, Q7, Q8, Q9, Q10, Q11, Q12, Q13, Q14, Q15, Q16, Q17, Q18, Q19, Q20, Q21, Q22, Q23, Q24, Q25, Q26, Q27, Q28, Q29, Q30, Q31]), "width" : 2 * mm, "tangentPropagation" : true});
        }
        {
            var Q0;
            {var subQ0=sQuery(id+"F4.wireOp",EDGE,"E24.left");Q0=makeQuery(id+"F4.imprint","IMPRINT",FACE,{"disambiguationData":[TD([[makeQuery(id+"F4.imprint","IMPRINT",EDGE,{"derivedFrom":subQ0}),-1.0]])]});}
            var Q1;
            {var subQ0=sQuery(id+"F4.wireOp",EDGE,"E24.top");Q1=makeQuery(id+"F4.imprint","IMPRINT",FACE,{"disambiguationData":[TD([[makeQuery(id+"F4.imprint","IMPRINT",EDGE,{"derivedFrom":subQ0}),-1.0]])]});}
            var Q2;
            {var subQ0=sQuery(id+"F4.wireOp",EDGE,"E24.right");Q2=makeQuery(id+"F4.imprint","IMPRINT",FACE,{"disambiguationData":[TD([[makeQuery(id+"F4.imprint","IMPRINT",EDGE,{"derivedFrom":subQ0}),1.0]])]});}
            var Q3;
            {var subQ1=sQuery(id+"F4.wireOp",EDGE,"E24.bottom");var subQ3=sQuery(id+"F4.wireOp",EDGE,"E33");var subQ4=makeQuery(id+"F4.imprint","INTERSECT",VERTEX,{"derivedFrom":[subQ1,subQ3]});Q3=makeQuery(id+"F4.imprint","IMPRINT",FACE,{"disambiguationData":[TD([[makeQuery(id+"F4.imprint","IMPRINT",EDGE,{"disambiguationData":[TD([[subQ4,-1.0]])],"derivedFrom":subQ3}),-1.0]])]});}
            var Q4;
            {var subQ1=sQuery(id+"F4.wireOp",EDGE,"E24.bottom");var subQ3=sQuery(id+"F4.wireOp",EDGE,"E33");var subQ4=makeQuery(id+"F4.imprint","INTERSECT",VERTEX,{"derivedFrom":[subQ1,subQ3]});Q4=makeQuery(id+"F4.imprint","IMPRINT",FACE,{"disambiguationData":[TD([[makeQuery(id+"F4.imprint","IMPRINT",EDGE,{"disambiguationData":[TD([[subQ4,-1.0]])],"derivedFrom":subQ3}),1.0]])]});}
            var Q5;
            {var subQ0=sQuery(id+"F4.wireOp",EDGE,"E34.1.16");Q5=makeQuery(id+"F4.imprint","IMPRINT",FACE,{"disambiguationData":[TD([[makeQuery(id+"F4.imprint","IMPRINT",EDGE,{"derivedFrom":subQ0}),-1.0]])]});}
            var Q6;
            {var subQ1=sQuery(id+"F4.wireOp",EDGE,"E34.1.3");var subQ3=sQuery(id+"F4.wireOp",EDGE,"E34.1.7");var subQ4=makeQuery(id+"F4.imprint","INTERSECT",VERTEX,{"derivedFrom":[subQ1,subQ3]});Q6=makeQuery(id+"F4.imprint","IMPRINT",FACE,{"disambiguationData":[TD([[makeQuery(id+"F4.imprint","IMPRINT",EDGE,{"disambiguationData":[TD([[subQ4,1.0]])],"derivedFrom":subQ1}),-1.0]])]});}
            var Q7;
            {var subQ0=sQuery(id+"F4.wireOp",EDGE,"E34.1.1");Q7=makeQuery(id+"F4.imprint","IMPRINT",FACE,{"disambiguationData":[TD([[makeQuery(id+"F4.imprint","IMPRINT",EDGE,{"derivedFrom":subQ0}),1.0]])]});}
            var Q8;
            {var subQ1=sQuery(id+"F4.wireOp",EDGE,"E34.1.5");var subQ3=sQuery(id+"F4.wireOp",EDGE,"E34.1.10");var subQ4=makeQuery(id+"F4.imprint","INTERSECT",VERTEX,{"derivedFrom":[subQ1,subQ3]});Q8=makeQuery(id+"F4.imprint","IMPRINT",FACE,{"disambiguationData":[TD([[makeQuery(id+"F4.imprint","IMPRINT",EDGE,{"disambiguationData":[TD([[subQ4,1.0]])],"derivedFrom":subQ3}),1.0]])]});}
            var Q9;
            {var subQ1=sQuery(id+"F4.wireOp",EDGE,"E34.2.3");var subQ3=sQuery(id+"F4.wireOp",EDGE,"E34.2.7");var subQ4=makeQuery(id+"F4.imprint","INTERSECT",VERTEX,{"derivedFrom":[subQ1,subQ3]});Q9=makeQuery(id+"F4.imprint","IMPRINT",FACE,{"disambiguationData":[TD([[makeQuery(id+"F4.imprint","IMPRINT",EDGE,{"disambiguationData":[TD([[subQ4,1.0]])],"derivedFrom":subQ1}),-1.0]])]});}
            var Q10;
            {var subQ1=sQuery(id+"F4.wireOp",EDGE,"E34.2.5");var subQ3=sQuery(id+"F4.wireOp",EDGE,"E34.2.10");var subQ4=makeQuery(id+"F4.imprint","INTERSECT",VERTEX,{"derivedFrom":[subQ1,subQ3]});Q10=makeQuery(id+"F4.imprint","IMPRINT",FACE,{"disambiguationData":[TD([[makeQuery(id+"F4.imprint","IMPRINT",EDGE,{"disambiguationData":[TD([[subQ4,1.0]])],"derivedFrom":subQ3}),1.0]])]});}
            var Q11;
            {var subQ0=sQuery(id+"F4.wireOp",EDGE,"E34.2.16");Q11=makeQuery(id+"F4.imprint","IMPRINT",FACE,{"disambiguationData":[TD([[makeQuery(id+"F4.imprint","IMPRINT",EDGE,{"derivedFrom":subQ0}),-1.0]])]});}
            var Q12;
            {var subQ0=sQuery(id+"F4.wireOp",EDGE,"E34.2.1");Q12=makeQuery(id+"F4.imprint","IMPRINT",FACE,{"disambiguationData":[TD([[makeQuery(id+"F4.imprint","IMPRINT",EDGE,{"derivedFrom":subQ0}),1.0]])]});}
            var Q13;
            {var subQ0=sQuery(id+"F4.wireOp",EDGE,"E35.37.6.0");Q13=makeQuery(id+"F4.imprint","IMPRINT",FACE,{"disambiguationData":[TD([[makeQuery(id+"F4.imprint","IMPRINT",EDGE,{"derivedFrom":subQ0}),1.0]])]});}
            var Q14;
            {var subQ0=sQuery(id+"F4.wireOp",EDGE,"E35.46.6.0");Q14=makeQuery(id+"F4.imprint","IMPRINT",FACE,{"disambiguationData":[TD([[makeQuery(id+"F4.imprint","IMPRINT",EDGE,{"derivedFrom":subQ0}),-1.0]])]});}
            var Q15;
            {var subQ1=sQuery(id+"F4.wireOp",EDGE,"E35.9.6.0");var subQ3=sQuery(id+"F4.wireOp",EDGE,"E35.19.6.0");var subQ4=makeQuery(id+"F4.imprint","INTERSECT",VERTEX,{"derivedFrom":[subQ1,subQ3]});Q15=makeQuery(id+"F4.imprint","IMPRINT",FACE,{"disambiguationData":[TD([[makeQuery(id+"F4.imprint","IMPRINT",EDGE,{"disambiguationData":[TD([[subQ4,1.0]])],"derivedFrom":subQ1}),-1.0]])]});}
            var Q16;
            {var subQ0=sQuery(id+"F4.wireOp",EDGE,"E35.3.6.0");Q16=makeQuery(id+"F4.imprint","IMPRINT",FACE,{"disambiguationData":[TD([[makeQuery(id+"F4.imprint","IMPRINT",EDGE,{"derivedFrom":subQ0}),1.0]])]});}
            var Q17;
            {var subQ0=sQuery(id+"F4.wireOp",EDGE,"E35.46.7.0");Q17=makeQuery(id+"F4.imprint","IMPRINT",FACE,{"disambiguationData":[TD([[makeQuery(id+"F4.imprint","IMPRINT",EDGE,{"derivedFrom":subQ0}),-1.0]])]});}
            var Q18;
            {var subQ1=sQuery(id+"F4.wireOp",EDGE,"E35.9.7.0");var subQ3=sQuery(id+"F4.wireOp",EDGE,"E35.19.7.0");var subQ4=makeQuery(id+"F4.imprint","INTERSECT",VERTEX,{"derivedFrom":[subQ1,subQ3]});Q18=makeQuery(id+"F4.imprint","IMPRINT",FACE,{"disambiguationData":[TD([[makeQuery(id+"F4.imprint","IMPRINT",EDGE,{"disambiguationData":[TD([[subQ4,1.0]])],"derivedFrom":subQ1}),-1.0]])]});}
            var Q19;
            {var subQ0=sQuery(id+"F4.wireOp",EDGE,"E35.3.7.0");Q19=makeQuery(id+"F4.imprint","IMPRINT",FACE,{"disambiguationData":[TD([[makeQuery(id+"F4.imprint","IMPRINT",EDGE,{"derivedFrom":subQ0}),1.0]])]});}
            var Q20;
            {var subQ0=sQuery(id+"F4.wireOp",EDGE,"E35.37.7.0");Q20=makeQuery(id+"F4.imprint","IMPRINT",FACE,{"disambiguationData":[TD([[makeQuery(id+"F4.imprint","IMPRINT",EDGE,{"derivedFrom":subQ0}),1.0]])]});}
            var Q21;
            {var subQ0=sQuery(id+"F4.wireOp",EDGE,"E35.37.5.0");Q21=makeQuery(id+"F4.imprint","IMPRINT",FACE,{"disambiguationData":[TD([[makeQuery(id+"F4.imprint","IMPRINT",EDGE,{"derivedFrom":subQ0}),1.0]])]});}
            var Q22;
            {var subQ0=sQuery(id+"F4.wireOp",EDGE,"E35.46.5.0");Q22=makeQuery(id+"F4.imprint","IMPRINT",FACE,{"disambiguationData":[TD([[makeQuery(id+"F4.imprint","IMPRINT",EDGE,{"derivedFrom":subQ0}),-1.0]])]});}
            var Q23;
            {var subQ1=sQuery(id+"F4.wireOp",EDGE,"E35.9.5.0");var subQ3=sQuery(id+"F4.wireOp",EDGE,"E35.19.5.0");var subQ4=makeQuery(id+"F4.imprint","INTERSECT",VERTEX,{"derivedFrom":[subQ1,subQ3]});Q23=makeQuery(id+"F4.imprint","IMPRINT",FACE,{"disambiguationData":[TD([[makeQuery(id+"F4.imprint","IMPRINT",EDGE,{"disambiguationData":[TD([[subQ4,1.0]])],"derivedFrom":subQ1}),-1.0]])]});}
            var Q24;
            {var subQ0=sQuery(id+"F4.wireOp",EDGE,"E35.3.5.0");Q24=makeQuery(id+"F4.imprint","IMPRINT",FACE,{"disambiguationData":[TD([[makeQuery(id+"F4.imprint","IMPRINT",EDGE,{"derivedFrom":subQ0}),1.0]])]});}
            var Q25;
            {var subQ0=sQuery(id+"F4.wireOp",EDGE,"E35.3.4.0");Q25=makeQuery(id+"F4.imprint","IMPRINT",FACE,{"disambiguationData":[TD([[makeQuery(id+"F4.imprint","IMPRINT",EDGE,{"derivedFrom":subQ0}),1.0]])]});}
            var Q26;
            {var subQ0=sQuery(id+"F4.wireOp",EDGE,"E35.37.4.0");Q26=makeQuery(id+"F4.imprint","IMPRINT",FACE,{"disambiguationData":[TD([[makeQuery(id+"F4.imprint","IMPRINT",EDGE,{"derivedFrom":subQ0}),1.0]])]});}
            var Q27;
            {var subQ0=sQuery(id+"F4.wireOp",EDGE,"E35.46.4.0");Q27=makeQuery(id+"F4.imprint","IMPRINT",FACE,{"disambiguationData":[TD([[makeQuery(id+"F4.imprint","IMPRINT",EDGE,{"derivedFrom":subQ0}),-1.0]])]});}
            var Q28;
            {var subQ1=sQuery(id+"F4.wireOp",EDGE,"E35.9.4.0");var subQ3=sQuery(id+"F4.wireOp",EDGE,"E35.19.4.0");var subQ4=makeQuery(id+"F4.imprint","INTERSECT",VERTEX,{"derivedFrom":[subQ1,subQ3]});Q28=makeQuery(id+"F4.imprint","IMPRINT",FACE,{"disambiguationData":[TD([[makeQuery(id+"F4.imprint","IMPRINT",EDGE,{"disambiguationData":[TD([[subQ4,1.0]])],"derivedFrom":subQ1}),-1.0]])]});}
            var Q29;
            {var subQ0=sQuery(id+"F4.wireOp",EDGE,"E35.3.3.0");Q29=makeQuery(id+"F4.imprint","IMPRINT",FACE,{"disambiguationData":[TD([[makeQuery(id+"F4.imprint","IMPRINT",EDGE,{"derivedFrom":subQ0}),1.0]])]});}
            var Q30;
            {var subQ0=sQuery(id+"F4.wireOp",EDGE,"E35.37.3.0");Q30=makeQuery(id+"F4.imprint","IMPRINT",FACE,{"disambiguationData":[TD([[makeQuery(id+"F4.imprint","IMPRINT",EDGE,{"derivedFrom":subQ0}),1.0]])]});}
            var Q31;
            {var subQ1=sQuery(id+"F4.wireOp",EDGE,"E35.9.3.0");var subQ3=sQuery(id+"F4.wireOp",EDGE,"E35.19.3.0");var subQ4=makeQuery(id+"F4.imprint","INTERSECT",VERTEX,{"derivedFrom":[subQ1,subQ3]});Q31=makeQuery(id+"F4.imprint","IMPRINT",FACE,{"disambiguationData":[TD([[makeQuery(id+"F4.imprint","IMPRINT",EDGE,{"disambiguationData":[TD([[subQ4,1.0]])],"derivedFrom":subQ1}),-1.0]])]});}
            var Q32;
            {var subQ0=sQuery(id+"F4.wireOp",EDGE,"E35.46.3.0");Q32=makeQuery(id+"F4.imprint","IMPRINT",FACE,{"disambiguationData":[TD([[makeQuery(id+"F4.imprint","IMPRINT",EDGE,{"derivedFrom":subQ0}),-1.0]])]});}
            extrude(context, id + "F7", {"entities" : qUnion([Q0, Q1, Q2, Q3, Q4, Q5, Q6, Q7, Q8, Q9, Q10, Q11, Q12, Q13, Q14, Q15, Q16, Q17, Q18, Q19, Q20, Q21, Q22, Q23, Q24, Q25, Q26, Q27, Q28, Q29, Q30, Q31, Q32]), "operationType" : NewBodyOperationType.REMOVE, "oppositeDirection" : true, "depth" : 25 * mm, "offsetDistance" : 25 * mm});
        }
        {
            var Q0;
            Q0=makeQuery(id+"F5.opExtrude","CAP_FACE",FACE,{"disambiguationData":[OSD([sQuery(id+"F4.wireOp",EDGE,"E20.bottom"),sQuery(id+"F4.wireOp",EDGE,"E20.top"),sQuery(id+"F4.wireOp",EDGE,"E20.left"),sQuery(id+"F4.wireOp",EDGE,"E20.right")])],"isStart":false});
            var Q1;
            Q1=makeQuery(id+"F5.opExtrude","CAP_FACE",FACE,{"disambiguationData":[OSD([sQuery(id+"F0.wireOp",EDGE,"E10.4"),sQuery(id+"F4.wireOp",EDGE,"E17.top"),sQuery(id+"F4.wireOp",EDGE,"E18.bottom"),sQuery(id+"F4.wireOp",EDGE,"E18.right"),sQuery(id+"F4.wireOp",EDGE,"E19.bottom"),sQuery(id+"F4.wireOp",EDGE,"E19.right")])],"isStart":false});
            var Q2;
            Q2=makeQuery(id+"F3.opExtrude","CAP_FACE",FACE,{"disambiguationData":[OSD([sQuery(id+"F0.wireOp",EDGE,"E11.5"),sQuery(id+"F0.wireOp",EDGE,"E11.6"),sQuery(id+"F0.wireOp",EDGE,"E13.5"),sQuery(id+"F0.wireOp",EDGE,"E13.6"),sQuery(id+"F0.wireOp",EDGE,"E14.right"),sQuery(id+"F0.wireOp",EDGE,"E15.1.1")])],"isStart":false});
            var Q3;
            Q3=makeQuery(id+"F2.opExtrude","CAP_FACE",FACE,{"disambiguationData":[OSD([sQuery(id+"F0.wireOp",EDGE,"E0.top"),sQuery(id+"F0.wireOp",EDGE,"E1.left"),sQuery(id+"F0.wireOp",EDGE,"E12.6"),sQuery(id+"F0.wireOp",EDGE,"E12.7"),sQuery(id+"F0.wireOp",EDGE,"E14.right"),sQuery(id+"F0.wireOp",EDGE,"E15.1.1")])],"isStart":false});
            var Q4;
            Q4=makeQuery(id+"F5.opExtrude","CAP_FACE",FACE,{"disambiguationData":[OSD([sQuery(id+"F4.wireOp",EDGE,"E22.1.2"),sQuery(id+"F4.wireOp",EDGE,"E22.1.15"),sQuery(id+"F4.wireOp",EDGE,"E22.1.16"),sQuery(id+"F4.wireOp",EDGE,"E22.1.20")])],"isStart":false});
            var Q5;
            Q5=makeQuery(id+"F5.opExtrude","CAP_FACE",FACE,{"disambiguationData":[OSD([sQuery(id+"F0.wireOp",EDGE,"E10.2"),sQuery(id+"F4.wireOp",EDGE,"E22.1.7"),sQuery(id+"F4.wireOp",EDGE,"E22.1.8"),sQuery(id+"F4.wireOp",EDGE,"E22.1.9"),sQuery(id+"F4.wireOp",EDGE,"E22.1.11"),sQuery(id+"F4.wireOp",EDGE,"E22.1.14")])],"isStart":false});
            var Q6;
            Q6=makeQuery(id+"F2.opExtrude","CAP_FACE",FACE,{"disambiguationData":[OSD([sQuery(id+"F0.wireOp",EDGE,"E0.left"),sQuery(id+"F0.wireOp",EDGE,"E1.left"),sQuery(id+"F0.wireOp",EDGE,"E12.3"),sQuery(id+"F0.wireOp",EDGE,"E12.7"),sQuery(id+"F0.wireOp",EDGE,"E15.1.3"),sQuery(id+"F0.wireOp",EDGE,"E15.2.1")])],"isStart":false});
            var Q7;
            Q7=makeQuery(id+"F3.opExtrude","CAP_FACE",FACE,{"disambiguationData":[OSD([sQuery(id+"F0.wireOp",EDGE,"E11.6"),sQuery(id+"F0.wireOp",EDGE,"E11.7"),sQuery(id+"F0.wireOp",EDGE,"E13.6"),sQuery(id+"F0.wireOp",EDGE,"E13.7"),sQuery(id+"F0.wireOp",EDGE,"E15.1.3"),sQuery(id+"F0.wireOp",EDGE,"E15.2.1")])],"isStart":false});
            var Q8;
            Q8=makeQuery(id+"F5.opExtrude","CAP_FACE",FACE,{"disambiguationData":[OSD([sQuery(id+"F4.wireOp",EDGE,"E22.1.0"),sQuery(id+"F4.wireOp",EDGE,"E22.1.3"),sQuery(id+"F4.wireOp",EDGE,"E22.1.13"),sQuery(id+"F4.wireOp",EDGE,"E22.1.19")])],"isStart":false});
            var Q9;
            Q9=makeQuery(id+"F5.opExtrude","CAP_FACE",FACE,{"disambiguationData":[OSD([sQuery(id+"F4.wireOp",EDGE,"E22.2.2"),sQuery(id+"F4.wireOp",EDGE,"E22.2.15"),sQuery(id+"F4.wireOp",EDGE,"E22.2.16"),sQuery(id+"F4.wireOp",EDGE,"E22.2.20")])],"isStart":false});
            var Q10;
            Q10=makeQuery(id+"F5.opExtrude","CAP_FACE",FACE,{"disambiguationData":[OSD([sQuery(id+"F0.wireOp",EDGE,"E10.0"),sQuery(id+"F4.wireOp",EDGE,"E22.2.7"),sQuery(id+"F4.wireOp",EDGE,"E22.2.8"),sQuery(id+"F4.wireOp",EDGE,"E22.2.9"),sQuery(id+"F4.wireOp",EDGE,"E22.2.11"),sQuery(id+"F4.wireOp",EDGE,"E22.2.14")])],"isStart":false});
            var Q11;
            Q11=makeQuery(id+"F5.opExtrude","CAP_FACE",FACE,{"disambiguationData":[OSD([sQuery(id+"F4.wireOp",EDGE,"E22.2.0"),sQuery(id+"F4.wireOp",EDGE,"E22.2.3"),sQuery(id+"F4.wireOp",EDGE,"E22.2.13"),sQuery(id+"F4.wireOp",EDGE,"E22.2.19")])],"isStart":false});
            var Q12;
            Q12=makeQuery(id+"F3.opExtrude","CAP_FACE",FACE,{"disambiguationData":[OSD([sQuery(id+"F0.wireOp",EDGE,"E11.3"),sQuery(id+"F0.wireOp",EDGE,"E11.7"),sQuery(id+"F0.wireOp",EDGE,"E13.3"),sQuery(id+"F0.wireOp",EDGE,"E13.7"),sQuery(id+"F0.wireOp",EDGE,"E15.2.3"),sQuery(id+"F0.wireOp",EDGE,"E16.3.3.0")])],"isStart":false});
            var Q13;
            Q13=makeQuery(id+"F2.opExtrude","CAP_FACE",FACE,{"disambiguationData":[OSD([sQuery(id+"F0.wireOp",EDGE,"E0.left"),sQuery(id+"F0.wireOp",EDGE,"E1.bottom"),sQuery(id+"F0.wireOp",EDGE,"E12.1"),sQuery(id+"F0.wireOp",EDGE,"E12.3"),sQuery(id+"F0.wireOp",EDGE,"E15.2.3"),sQuery(id+"F0.wireOp",EDGE,"E16.3.3.0")])],"isStart":false});
            var Q14;
            Q14=makeQuery(id+"F5.opExtrude","CAP_FACE",FACE,{"disambiguationData":[OSD([sQuery(id+"F4.wireOp",EDGE,"E23.6.3.0"),sQuery(id+"F4.wireOp",EDGE,"E23.43.3.0"),sQuery(id+"F4.wireOp",EDGE,"E23.46.3.0"),sQuery(id+"F4.wireOp",EDGE,"E23.56.3.0")])],"isStart":false});
            var Q15;
            Q15=makeQuery(id+"F5.opExtrude","CAP_FACE",FACE,{"disambiguationData":[OSD([sQuery(id+"F0.wireOp",EDGE,"E10.1"),sQuery(id+"F4.wireOp",EDGE,"E23.19.3.0"),sQuery(id+"F4.wireOp",EDGE,"E23.22.3.0"),sQuery(id+"F4.wireOp",EDGE,"E23.25.3.0"),sQuery(id+"F4.wireOp",EDGE,"E23.31.3.0"),sQuery(id+"F4.wireOp",EDGE,"E23.40.3.0")])],"isStart":false});
            var Q16;
            Q16=makeQuery(id+"F5.opExtrude","CAP_FACE",FACE,{"disambiguationData":[OSD([sQuery(id+"F4.wireOp",EDGE,"E23.9.3.0"),sQuery(id+"F4.wireOp",EDGE,"E23.24.3.0"),sQuery(id+"F4.wireOp",EDGE,"E23.37.3.0"),sQuery(id+"F4.wireOp",EDGE,"E23.53.3.0")])],"isStart":false});
            var Q17;
            Q17=makeQuery(id+"F3.opExtrude","CAP_FACE",FACE,{"disambiguationData":[OSD([sQuery(id+"F0.wireOp",EDGE,"E11.1"),sQuery(id+"F0.wireOp",EDGE,"E11.3"),sQuery(id+"F0.wireOp",EDGE,"E13.1"),sQuery(id+"F0.wireOp",EDGE,"E13.3"),sQuery(id+"F0.wireOp",EDGE,"E16.9.3.0"),sQuery(id+"F0.wireOp",EDGE,"E16.3.4.0")])],"isStart":false});
            var Q18;
            Q18=makeQuery(id+"F2.opExtrude","CAP_FACE",FACE,{"disambiguationData":[OSD([sQuery(id+"F0.wireOp",EDGE,"E0.bottom"),sQuery(id+"F0.wireOp",EDGE,"E1.bottom"),sQuery(id+"F0.wireOp",EDGE,"E12.0"),sQuery(id+"F0.wireOp",EDGE,"E12.1"),sQuery(id+"F0.wireOp",EDGE,"E16.9.3.0"),sQuery(id+"F0.wireOp",EDGE,"E16.3.4.0")])],"isStart":false});
            var Q19;
            Q19=makeQuery(id+"F5.opExtrude","CAP_FACE",FACE,{"disambiguationData":[OSD([sQuery(id+"F4.wireOp",EDGE,"E23.6.4.0"),sQuery(id+"F4.wireOp",EDGE,"E23.43.4.0"),sQuery(id+"F4.wireOp",EDGE,"E23.46.4.0"),sQuery(id+"F4.wireOp",EDGE,"E23.56.4.0")])],"isStart":false});
            var Q20;
            Q20=makeQuery(id+"F5.opExtrude","CAP_FACE",FACE,{"disambiguationData":[OSD([sQuery(id+"F0.wireOp",EDGE,"E10.3"),sQuery(id+"F4.wireOp",EDGE,"E23.19.4.0"),sQuery(id+"F4.wireOp",EDGE,"E23.22.4.0"),sQuery(id+"F4.wireOp",EDGE,"E23.25.4.0"),sQuery(id+"F4.wireOp",EDGE,"E23.31.4.0"),sQuery(id+"F4.wireOp",EDGE,"E23.40.4.0")])],"isStart":false});
            var Q21;
            Q21=makeQuery(id+"F3.opExtrude","CAP_FACE",FACE,{"disambiguationData":[OSD([sQuery(id+"F0.wireOp",EDGE,"E11.0"),sQuery(id+"F0.wireOp",EDGE,"E11.1"),sQuery(id+"F0.wireOp",EDGE,"E13.0"),sQuery(id+"F0.wireOp",EDGE,"E13.1"),sQuery(id+"F0.wireOp",EDGE,"E16.9.4.0"),sQuery(id+"F0.wireOp",EDGE,"E16.3.5.0")])],"isStart":false});
            var Q22;
            Q22=makeQuery(id+"F2.opExtrude","CAP_FACE",FACE,{"disambiguationData":[OSD([sQuery(id+"F0.wireOp",EDGE,"E0.bottom"),sQuery(id+"F0.wireOp",EDGE,"E1.right"),sQuery(id+"F0.wireOp",EDGE,"E12.0"),sQuery(id+"F0.wireOp",EDGE,"E12.2"),sQuery(id+"F0.wireOp",EDGE,"E16.9.4.0"),sQuery(id+"F0.wireOp",EDGE,"E16.3.5.0")])],"isStart":false});
            var Q23;
            Q23=makeQuery(id+"F5.opExtrude","CAP_FACE",FACE,{"disambiguationData":[OSD([sQuery(id+"F4.wireOp",EDGE,"E23.9.4.0"),sQuery(id+"F4.wireOp",EDGE,"E23.24.4.0"),sQuery(id+"F4.wireOp",EDGE,"E23.37.4.0"),sQuery(id+"F4.wireOp",EDGE,"E23.53.4.0")])],"isStart":false});
            var Q24;
            Q24=makeQuery(id+"F5.opExtrude","CAP_FACE",FACE,{"disambiguationData":[OSD([sQuery(id+"F4.wireOp",EDGE,"E23.6.5.0"),sQuery(id+"F4.wireOp",EDGE,"E23.43.5.0"),sQuery(id+"F4.wireOp",EDGE,"E23.46.5.0"),sQuery(id+"F4.wireOp",EDGE,"E23.56.5.0")])],"isStart":false});
            var Q25;
            Q25=makeQuery(id+"F5.opExtrude","CAP_FACE",FACE,{"disambiguationData":[OSD([sQuery(id+"F0.wireOp",EDGE,"E10.7"),sQuery(id+"F4.wireOp",EDGE,"E23.19.5.0"),sQuery(id+"F4.wireOp",EDGE,"E23.22.5.0"),sQuery(id+"F4.wireOp",EDGE,"E23.25.5.0"),sQuery(id+"F4.wireOp",EDGE,"E23.31.5.0"),sQuery(id+"F4.wireOp",EDGE,"E23.40.5.0")])],"isStart":false});
            var Q26;
            Q26=makeQuery(id+"F5.opExtrude","CAP_FACE",FACE,{"disambiguationData":[OSD([sQuery(id+"F4.wireOp",EDGE,"E23.9.5.0"),sQuery(id+"F4.wireOp",EDGE,"E23.24.5.0"),sQuery(id+"F4.wireOp",EDGE,"E23.37.5.0"),sQuery(id+"F4.wireOp",EDGE,"E23.53.5.0")])],"isStart":false});
            var Q27;
            Q27=makeQuery(id+"F3.opExtrude","CAP_FACE",FACE,{"disambiguationData":[OSD([sQuery(id+"F0.wireOp",EDGE,"E11.0"),sQuery(id+"F0.wireOp",EDGE,"E11.2"),sQuery(id+"F0.wireOp",EDGE,"E13.0"),sQuery(id+"F0.wireOp",EDGE,"E13.2"),sQuery(id+"F0.wireOp",EDGE,"E16.9.5.0"),sQuery(id+"F0.wireOp",EDGE,"E16.3.6.0")])],"isStart":false});
            var Q28;
            Q28=makeQuery(id+"F2.opExtrude","CAP_FACE",FACE,{"disambiguationData":[OSD([sQuery(id+"F0.wireOp",EDGE,"E0.right"),sQuery(id+"F0.wireOp",EDGE,"E1.right"),sQuery(id+"F0.wireOp",EDGE,"E12.2"),sQuery(id+"F0.wireOp",EDGE,"E12.4"),sQuery(id+"F0.wireOp",EDGE,"E16.9.5.0"),sQuery(id+"F0.wireOp",EDGE,"E16.3.6.0")])],"isStart":false});
            var Q29;
            Q29=makeQuery(id+"F5.opExtrude","CAP_FACE",FACE,{"disambiguationData":[OSD([sQuery(id+"F4.wireOp",EDGE,"E23.6.6.0"),sQuery(id+"F4.wireOp",EDGE,"E23.43.6.0"),sQuery(id+"F4.wireOp",EDGE,"E23.46.6.0"),sQuery(id+"F4.wireOp",EDGE,"E23.56.6.0")])],"isStart":false});
            var Q30;
            Q30=makeQuery(id+"F5.opExtrude","CAP_FACE",FACE,{"disambiguationData":[OSD([sQuery(id+"F0.wireOp",EDGE,"E10.6"),sQuery(id+"F4.wireOp",EDGE,"E23.19.6.0"),sQuery(id+"F4.wireOp",EDGE,"E23.22.6.0"),sQuery(id+"F4.wireOp",EDGE,"E23.25.6.0"),sQuery(id+"F4.wireOp",EDGE,"E23.31.6.0"),sQuery(id+"F4.wireOp",EDGE,"E23.40.6.0")])],"isStart":false});
            var Q31;
            Q31=makeQuery(id+"F3.opExtrude","CAP_FACE",FACE,{"disambiguationData":[OSD([sQuery(id+"F0.wireOp",EDGE,"E11.2"),sQuery(id+"F0.wireOp",EDGE,"E11.4"),sQuery(id+"F0.wireOp",EDGE,"E13.2"),sQuery(id+"F0.wireOp",EDGE,"E13.4"),sQuery(id+"F0.wireOp",EDGE,"E16.9.6.0"),sQuery(id+"F0.wireOp",EDGE,"E16.3.7.0")])],"isStart":false});
            var Q32;
            Q32=makeQuery(id+"F5.opExtrude","CAP_FACE",FACE,{"disambiguationData":[OSD([sQuery(id+"F4.wireOp",EDGE,"E23.6.7.0"),sQuery(id+"F4.wireOp",EDGE,"E23.43.7.0"),sQuery(id+"F4.wireOp",EDGE,"E23.46.7.0"),sQuery(id+"F4.wireOp",EDGE,"E23.56.7.0")])],"isStart":false});
            var Q33;
            Q33=makeQuery(id+"F5.opExtrude","CAP_FACE",FACE,{"disambiguationData":[OSD([sQuery(id+"F4.wireOp",EDGE,"E23.9.7.0"),sQuery(id+"F4.wireOp",EDGE,"E23.24.7.0"),sQuery(id+"F4.wireOp",EDGE,"E23.37.7.0"),sQuery(id+"F4.wireOp",EDGE,"E23.53.7.0")])],"isStart":false});
            var Q34;
            Q34=makeQuery(id+"F3.opExtrude","CAP_FACE",FACE,{"disambiguationData":[OSD([sQuery(id+"F0.wireOp",EDGE,"E11.4"),sQuery(id+"F0.wireOp",EDGE,"E11.5"),sQuery(id+"F0.wireOp",EDGE,"E13.4"),sQuery(id+"F0.wireOp",EDGE,"E13.5"),sQuery(id+"F0.wireOp",EDGE,"E14.left"),sQuery(id+"F0.wireOp",EDGE,"E16.9.7.0")])],"isStart":false});
            var Q35;
            Q35=makeQuery(id+"F2.opExtrude","CAP_FACE",FACE,{"disambiguationData":[OSD([sQuery(id+"F0.wireOp",EDGE,"E0.top"),sQuery(id+"F0.wireOp",EDGE,"E1.top"),sQuery(id+"F0.wireOp",EDGE,"E12.5"),sQuery(id+"F0.wireOp",EDGE,"E12.6"),sQuery(id+"F0.wireOp",EDGE,"E14.left"),sQuery(id+"F0.wireOp",EDGE,"E16.9.7.0")])],"isStart":false});
            var Q36;
            Q36=makeQuery(id+"F5.opExtrude","CAP_FACE",FACE,{"disambiguationData":[OSD([sQuery(id+"F4.wireOp",EDGE,"E19.top"),sQuery(id+"F4.wireOp",EDGE,"E21.top"),sQuery(id+"F4.wireOp",EDGE,"E21.left"),sQuery(id+"F4.wireOp",EDGE,"E21.right")])],"isStart":false});
            var Q37;
            Q37=makeQuery(id+"F5.opExtrude","CAP_FACE",FACE,{"disambiguationData":[OSD([sQuery(id+"F0.wireOp",EDGE,"E10.5"),sQuery(id+"F4.wireOp",EDGE,"E23.19.7.0"),sQuery(id+"F4.wireOp",EDGE,"E23.22.7.0"),sQuery(id+"F4.wireOp",EDGE,"E23.25.7.0"),sQuery(id+"F4.wireOp",EDGE,"E23.31.7.0"),sQuery(id+"F4.wireOp",EDGE,"E23.40.7.0")])],"isStart":false});
            var Q38;
            Q38=makeQuery(id+"F5.opExtrude","CAP_FACE",FACE,{"disambiguationData":[OSD([sQuery(id+"F4.wireOp",EDGE,"E23.9.6.0"),sQuery(id+"F4.wireOp",EDGE,"E23.24.6.0"),sQuery(id+"F4.wireOp",EDGE,"E23.37.6.0"),sQuery(id+"F4.wireOp",EDGE,"E23.53.6.0")])],"isStart":false});
            var Q39;
            Q39=makeQuery(id+"F2.opExtrude","CAP_FACE",FACE,{"disambiguationData":[OSD([sQuery(id+"F0.wireOp",EDGE,"E0.right"),sQuery(id+"F0.wireOp",EDGE,"E1.top"),sQuery(id+"F0.wireOp",EDGE,"E12.4"),sQuery(id+"F0.wireOp",EDGE,"E12.5"),sQuery(id+"F0.wireOp",EDGE,"E16.9.6.0"),sQuery(id+"F0.wireOp",EDGE,"E16.3.7.0")])],"isStart":false});
            chamfer(context, id + "F8", {"entities" : qUnion([Q0, Q1, Q2, Q3, Q4, Q5, Q6, Q7, Q8, Q9, Q10, Q11, Q12, Q13, Q14, Q15, Q16, Q17, Q18, Q19, Q20, Q21, Q22, Q23, Q24, Q25, Q26, Q27, Q28, Q29, Q30, Q31, Q32, Q33, Q34, Q35, Q36, Q37, Q38, Q39]), "width" : .5 * mm, "tangentPropagation" : true});
        }
    });
